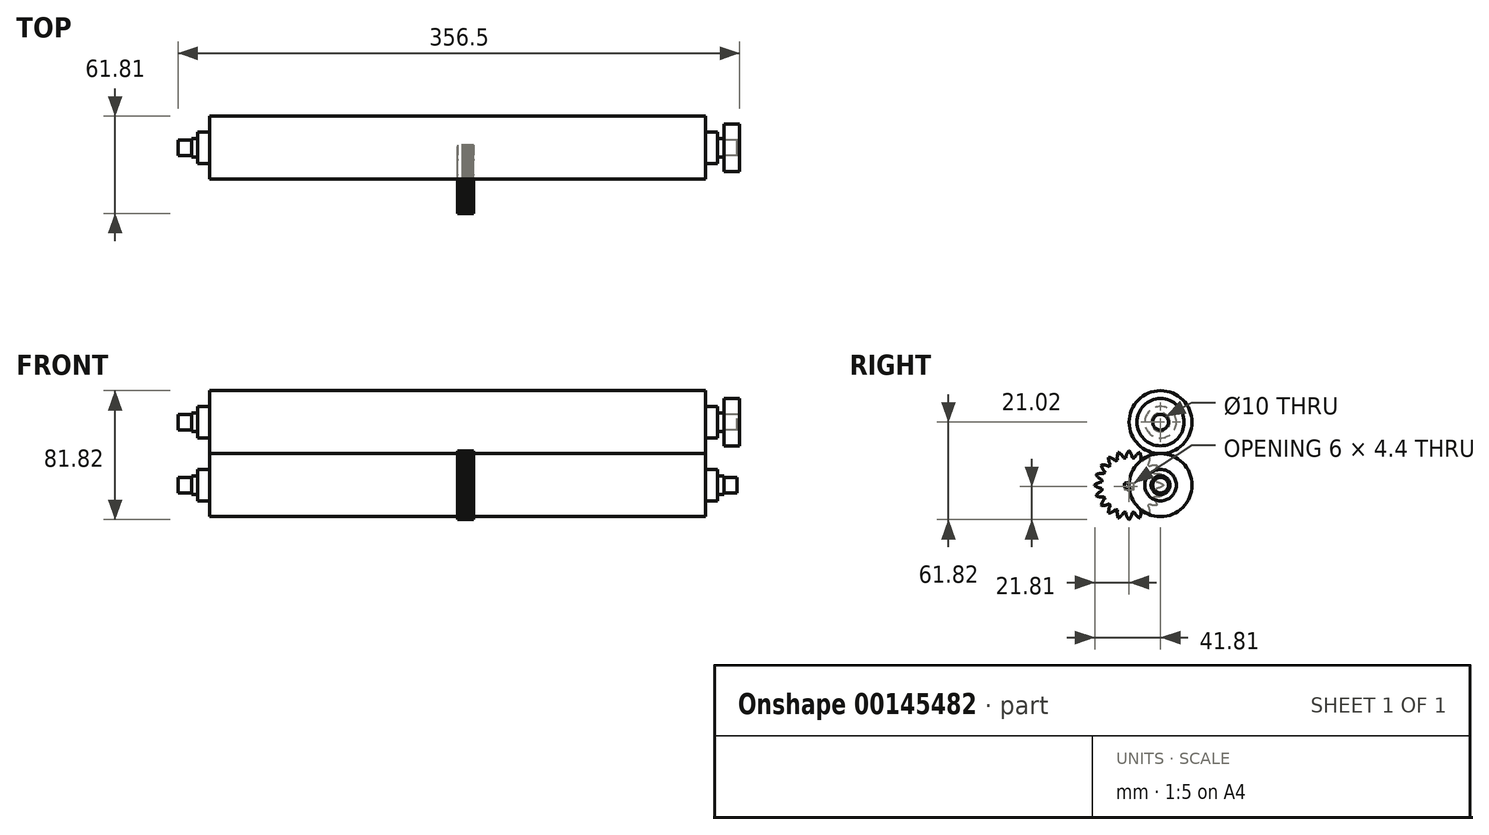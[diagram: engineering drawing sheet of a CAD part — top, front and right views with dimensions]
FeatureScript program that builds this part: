
annotation { "Feature Type Name" : "Feature", "Feature Type Description" : "" }
export const myFeature = defineFeature(function(context is Context, id is Id, definition is map)
    precondition{}
    {
        {
            var Q0;
            Q0=qCreatedBy(makeId("Right.planeOp"),FACE);
            var sketch = newSketch(context, id + "F0", { "sketchPlane" : qUnion([Q0])});
            skCircle(sketch, "E0", {"center": v(0, 0) * mm, "radius": 20 * mm});
            skCircle(sketch, "E1", {"center": v(0, 0) * mm, "radius": 10 * mm});
            skCircle(sketch, "E2", {"center": v(0, 0) * mm, "radius": 5 * mm});
            skCircle(sketch, "E3", {"center": v(0, 0) * mm, "radius": 6 * mm});
            skSolve(sketch);
        }
        {
            var Q0;
            Q0=makeQuery(id+"F0.imprint","IMPRINT",FACE,{"disambiguationData":[TD([[makeQuery(id+"F0.imprint","IMPRINT",EDGE,{"derivedFrom":sQuery(id+"F0.wireOp",EDGE,"E0")}),1.0]])]});
            extrude(context, id + "F1", {"entities" : qUnion([Q0]), "endBound" : BoundingType.SYMMETRIC, "depth" : 315 * mm});
        }
        {
            var Q0;
            Q0=makeQuery(id+"F0.imprint","IMPRINT",FACE,{"disambiguationData":[TD([[makeQuery(id+"F0.imprint","IMPRINT",EDGE,{"derivedFrom":sQuery(id+"F0.wireOp",EDGE,"E1")}),1.0]])]});
            extrude(context, id + "F2", {"entities" : qUnion([Q0]), "operationType" : NewBodyOperationType.ADD, "endBound" : BoundingType.SYMMETRIC, "depth" : 330 * mm});
        }
        {
            var Q0;
            Q0=makeQuery(id+"F0.imprint","IMPRINT",FACE,{"disambiguationData":[TD([[makeQuery(id+"F0.imprint","IMPRINT",EDGE,{"derivedFrom":sQuery(id+"F0.wireOp",EDGE,"E2")}),-1.0]])]});
            extrude(context, id + "F3", {"entities" : qUnion([Q0]), "operationType" : NewBodyOperationType.ADD, "endBound" : BoundingType.SYMMETRIC, "depth" : 338 * mm});
        }
        {
            var Q0;
            Q0=makeQuery(id+"F0.imprint","IMPRINT",FACE,{"disambiguationData":[TD([[makeQuery(id+"F0.imprint","IMPRINT",EDGE,{"derivedFrom":sQuery(id+"F0.wireOp",EDGE,"E2")}),1.0]])]});
            extrude(context, id + "F4", {"entities" : qUnion([Q0]), "operationType" : NewBodyOperationType.ADD, "endBound" : BoundingType.SYMMETRIC, "depth" : 355 * mm});
        }
        {
            var Q0;
            Q0=makeQuery(id+"F1.opExtrude","SWEPT_BODY",BODY,{"disambiguationData":[OSD([sQuery(id+"F0.wireOp",EDGE,"E0"),sQuery(id+"F0.wireOp",EDGE,"E1")])]});
            transform(context, id + "F5", {"entities" : qUnion([Q0]), "transformType" : TransformType.TRANSLATION_3D, "dx" : 0 * mm, "dy" : 0 * mm, "dz" : 40 * mm, "makeCopy" : true});
        }
        {
            var Q0;
            Q0=makeQuery(id+"F3.opExtrude","CAP_FACE",FACE,{"disambiguationData":[OSD([sQuery(id+"F0.wireOp",EDGE,"E2"),sQuery(id+"F0.wireOp",EDGE,"E3")])],"isStart":false});
            var sketch = newSketch(context, id + "F6", { "sketchPlane" : qUnion([Q0])});
            skLineSegment(sketch, "E4", {"start": v(0, 69.94) * mm, "end": v(0, -29.94) * mm, "construction": true});
            skLineSegment(sketch, "E5", {"start": v(-33.24, 0) * mm, "end": v(34.61, 0) * mm, "construction": true});
            skLineSegment(sketch, "E6", {"start": v(-30.84, 40) * mm, "end": v(31.61, 40) * mm, "construction": true});
            skCircle(sketch, "E7", {"center": v(0, 40) * mm, "radius": 5 * mm});
            skCircle(sketch, "E8", {"center": v(0, 0) * mm, "radius": 5 * mm});
            skLineSegment(sketch, "E9", {"start": v(-34.27, 20) * mm, "end": v(43.16, 20) * mm, "construction": true});
            skPoint(sketch, "E9.startSnap0", {"position": v(0, 20) * mm});
            skCircle(sketch, "E10", {"center": v(0, 40) * mm, "radius": 15 * mm});
            skSolve(sketch);
        }
        {
            var Q0;
            Q0=makeQuery(id+"F6.imprint","IMPRINT",FACE,{"disambiguationData":[TD([[makeQuery(id+"F6.imprint","IMPRINT",EDGE,{"derivedFrom":sQuery(id+"F6.wireOp",EDGE,"E7")}),-1.0]])]});
            extrude(context, id + "F7", {"entities" : qUnion([Q0]), "depth" : 10 * mm});
        }
        {
            var Q0;
            Q0=qCreatedBy(makeId("Right.planeOp"),FACE);
            var sketch = newSketch(context, id + "F8", { "sketchPlane" : qUnion([Q0])});
            skCircle(sketch, "E11.cCircle", {"center": v(-47.34, 46.55) * mm, "radius": 11.16 * mm, "construction": true});
            skLineSegment(sketch, "E11.0", {"start": v(-38.6, 37.07) * mm, "end": v(-51.18, 34.24) * mm});
            skLineSegment(sketch, "E11.1", {"start": v(-51.18, 34.24) * mm, "end": v(-59.91, 43.72) * mm});
            skLineSegment(sketch, "E11.2", {"start": v(-59.91, 43.72) * mm, "end": v(-56.07, 56.02) * mm});
            skLineSegment(sketch, "E11.3", {"start": v(-56.07, 56.02) * mm, "end": v(-43.5, 58.85) * mm});
            skLineSegment(sketch, "E11.4", {"start": v(-43.5, 58.85) * mm, "end": v(-34.77, 49.38) * mm});
            skLineSegment(sketch, "E11.5", {"start": v(-34.77, 49.38) * mm, "end": v(-38.6, 37.07) * mm});
            skPoint(sketch, "E11.0.midPoint", {"position": v(-44.89, 35.66) * mm});
            skSolve(sketch);
        }
        {
            var Q0;
            Q0=makeQuery(id+"F8.imprint","IMPRINT",FACE,{"disambiguationData":[TD([[makeQuery(id+"F8.imprint","IMPRINT",EDGE,{"derivedFrom":sQuery(id+"F8.wireOp",EDGE,"E11.0")}),-1.0]])]});
            extrude(context, id + "F9", {"entities" : qUnion([Q0]), "depth" : 25 * mm});
        }
        {
            var Q0;
            Q0=makeQuery(id+"F9.opExtrude","SWEPT_BODY",BODY,{"disambiguationData":[OSD([sQuery(id+"F8.wireOp",EDGE,"E11.0"),sQuery(id+"F8.wireOp",EDGE,"E11.1"),sQuery(id+"F8.wireOp",EDGE,"E11.2"),sQuery(id+"F8.wireOp",EDGE,"E11.3"),sQuery(id+"F8.wireOp",EDGE,"E11.4"),sQuery(id+"F8.wireOp",EDGE,"E11.5")])]});
            transform(context, id + "F10", {"entities" : qUnion([Q0]), "transformType" : TransformType.TRANSLATION_3D, "dx" : -53.2 * mm, "dy" : 0 * mm, "dz" : 0 * mm, "makeCopy" : true});
        }
        {
            var Q0;
            Q0=makeQuery(id+"F10.opPattern","COPY",BODY,{"derivedFrom":makeQuery(id+"F9.opExtrude","SWEPT_BODY",BODY,{"disambiguationData":[OSD([sQuery(id+"F8.wireOp",EDGE,"E11.0"),sQuery(id+"F8.wireOp",EDGE,"E11.1"),sQuery(id+"F8.wireOp",EDGE,"E11.2"),sQuery(id+"F8.wireOp",EDGE,"E11.3"),sQuery(id+"F8.wireOp",EDGE,"E11.4"),sQuery(id+"F8.wireOp",EDGE,"E11.5")])]}),"instanceName":"1"});
            var Q1;
            Q1=makeQuery(id+"F10.opPattern","COPY",EDGE,{"derivedFrom":makeQuery(id+"F9.opExtrude","SWEPT_EDGE",EDGE,{"disambiguationData":[OSD([sQuery(id+"F8.wireOp",EDGE,"E11.0"),sQuery(id+"F8.wireOp",EDGE,"E11.1")])]}),"instanceName":"1"});
            transform(context, id + "F11", {"entities" : qUnion([Q0]), "transformType" : TransformType.ROTATION, "transformAxis" : qUnion([Q1]), "angle" : 30 * degree, "makeCopy" : false});
        }
        {
            var Q0;
            Q0=makeQuery(id+"F10.opPattern","COPY",FACE,{"derivedFrom":makeQuery(id+"F9.opExtrude","CAP_FACE",FACE,{"disambiguationData":[OSD([sQuery(id+"F8.wireOp",EDGE,"E11.0"),sQuery(id+"F8.wireOp",EDGE,"E11.1"),sQuery(id+"F8.wireOp",EDGE,"E11.2"),sQuery(id+"F8.wireOp",EDGE,"E11.3"),sQuery(id+"F8.wireOp",EDGE,"E11.4"),sQuery(id+"F8.wireOp",EDGE,"E11.5")])],"isStart":false}),"instanceName":"1"});
            var Q1;
            Q1=makeQuery(id+"F9.opExtrude","CAP_FACE",FACE,{"disambiguationData":[OSD([sQuery(id+"F8.wireOp",EDGE,"E11.0"),sQuery(id+"F8.wireOp",EDGE,"E11.1"),sQuery(id+"F8.wireOp",EDGE,"E11.2"),sQuery(id+"F8.wireOp",EDGE,"E11.3"),sQuery(id+"F8.wireOp",EDGE,"E11.4"),sQuery(id+"F8.wireOp",EDGE,"E11.5")])],"isStart":true});
            loft(context, id + "F12", {"sheetProfilesArray" : [{ "sheetProfileEntities" : qUnion([Q0]) }, { "sheetProfileEntities" : qUnion([Q1]) }]});
        }
        {
            var Q0;
            Q0=makeQuery(id+"F12.opLoft","SWEPT_BODY",BODY,{"disambiguationData":[OSD([sQuery(id+"F8.wireOp",EDGE,"E11.0"),sQuery(id+"F8.wireOp",EDGE,"E11.1"),sQuery(id+"F8.wireOp",EDGE,"E11.2"),sQuery(id+"F8.wireOp",EDGE,"E11.3"),sQuery(id+"F8.wireOp",EDGE,"E11.4"),sQuery(id+"F8.wireOp",EDGE,"E11.5")])]});
            deleteBodies(context, id + "F13", {"entities" : qUnion([Q0])});
        }
        {
            var Q0;
            Q0=makeQuery(id+"F10.opPattern","COPY",BODY,{"derivedFrom":makeQuery(id+"F9.opExtrude","SWEPT_BODY",BODY,{"disambiguationData":[OSD([sQuery(id+"F8.wireOp",EDGE,"E11.0"),sQuery(id+"F8.wireOp",EDGE,"E11.1"),sQuery(id+"F8.wireOp",EDGE,"E11.2"),sQuery(id+"F8.wireOp",EDGE,"E11.3"),sQuery(id+"F8.wireOp",EDGE,"E11.4"),sQuery(id+"F8.wireOp",EDGE,"E11.5")])]}),"instanceName":"1"});
            deleteBodies(context, id + "F14", {"entities" : qUnion([Q0])});
        }
        {
            var Q0;
            Q0=makeQuery(id+"F9.opExtrude","SWEPT_BODY",BODY,{"disambiguationData":[OSD([sQuery(id+"F8.wireOp",EDGE,"E11.0"),sQuery(id+"F8.wireOp",EDGE,"E11.1"),sQuery(id+"F8.wireOp",EDGE,"E11.2"),sQuery(id+"F8.wireOp",EDGE,"E11.3"),sQuery(id+"F8.wireOp",EDGE,"E11.4"),sQuery(id+"F8.wireOp",EDGE,"E11.5")])]});
            deleteBodies(context, id + "F15", {"entities" : qUnion([Q0])});
        }
        {
            var Q0;
            Q0=qCreatedBy(makeId("Right.planeOp"),FACE);
            var sketch = newSketch(context, id + "F16", { "sketchPlane" : qUnion([Q0])});
            skLineSegment(sketch, "E12", {"start": v(-0.26, 0.2) * mm, "end": v(-0.26, 0.2) * mm});
            skLineSegment(sketch, "E13", {"start": v(-0.26, 0.2) * mm, "end": v(-0.25, 0.2) * mm});
            skLineSegment(sketch, "E14", {"start": v(-0.25, 0.2) * mm, "end": v(-0.24, 0.2) * mm});
            skLineSegment(sketch, "E15", {"start": v(-0.24, 0.2) * mm, "end": v(-0.23, 0.2) * mm});
            skLineSegment(sketch, "E16", {"start": v(-0.23, 0.2) * mm, "end": v(-0.23, 0.2) * mm});
            skLineSegment(sketch, "E17", {"start": v(-0.23, 0.2) * mm, "end": v(-0.22, 0.2) * mm});
            skLineSegment(sketch, "E18", {"start": v(-0.22, 0.2) * mm, "end": v(-0.2, 0.2) * mm});
            skLineSegment(sketch, "E19", {"start": v(-0.2, 0.2) * mm, "end": v(-0.18, 0.2) * mm});
            skLineSegment(sketch, "E20", {"start": v(-0.18, 0.2) * mm, "end": v(-0.17, 0.2) * mm});
            skLineSegment(sketch, "E21", {"start": v(-0.17, 0.2) * mm, "end": v(-0.14, 0.19) * mm});
            skLineSegment(sketch, "E22", {"start": v(-0.14, 0.19) * mm, "end": v(-0.1, 0.18) * mm});
            skLineSegment(sketch, "E23", {"start": v(-0.1, 0.18) * mm, "end": v(-0.07, 0.16) * mm});
            skLineSegment(sketch, "E24", {"start": v(-0.07, 0.16) * mm, "end": v(-0.04, 0.15) * mm});
            skLineSegment(sketch, "E25", {"start": v(-0.04, 0.15) * mm, "end": v(0, 0.14) * mm});
            skLineSegment(sketch, "E26", {"start": v(0, 0.14) * mm, "end": v(0.02, 0.12) * mm});
            skLineSegment(sketch, "E27", {"start": v(0.02, 0.12) * mm, "end": v(0.06, 0.1) * mm});
            skLineSegment(sketch, "E28", {"start": v(0.06, 0.1) * mm, "end": v(0.09, 0.08) * mm});
            skLineSegment(sketch, "E29", {"start": v(0.09, 0.08) * mm, "end": v(0.12, 0.06) * mm});
            skLineSegment(sketch, "E30", {"start": v(0.12, 0.06) * mm, "end": v(0.15, 0.04) * mm});
            skLineSegment(sketch, "E31", {"start": v(0.15, 0.04) * mm, "end": v(0.18, 0.02) * mm});
            skLineSegment(sketch, "E32", {"start": v(0.18, 0.02) * mm, "end": v(0.18, -0.02) * mm});
            skLineSegment(sketch, "E33", {"start": v(0.18, -0.02) * mm, "end": v(0.15, -0.04) * mm});
            skLineSegment(sketch, "E34", {"start": v(0.15, -0.04) * mm, "end": v(0.12, -0.06) * mm});
            skLineSegment(sketch, "E35", {"start": v(0.12, -0.06) * mm, "end": v(0.09, -0.08) * mm});
            skLineSegment(sketch, "E36", {"start": v(0.09, -0.08) * mm, "end": v(0.06, -0.1) * mm});
            skLineSegment(sketch, "E37", {"start": v(0.06, -0.1) * mm, "end": v(0.02, -0.12) * mm});
            skLineSegment(sketch, "E38", {"start": v(0.02, -0.12) * mm, "end": v(0, -0.14) * mm});
            skLineSegment(sketch, "E39", {"start": v(0, -0.14) * mm, "end": v(-0.04, -0.15) * mm});
            skLineSegment(sketch, "E40", {"start": v(-0.04, -0.15) * mm, "end": v(-0.07, -0.16) * mm});
            skLineSegment(sketch, "E41", {"start": v(-0.07, -0.16) * mm, "end": v(-0.1, -0.18) * mm});
            skLineSegment(sketch, "E42", {"start": v(-0.1, -0.18) * mm, "end": v(-0.14, -0.19) * mm});
            skLineSegment(sketch, "E43", {"start": v(-0.14, -0.19) * mm, "end": v(-0.17, -0.2) * mm});
            skLineSegment(sketch, "E44", {"start": v(-0.17, -0.2) * mm, "end": v(-0.18, -0.2) * mm});
            skLineSegment(sketch, "E45", {"start": v(-0.18, -0.2) * mm, "end": v(-0.2, -0.2) * mm});
            skLineSegment(sketch, "E46", {"start": v(-0.2, -0.2) * mm, "end": v(-0.22, -0.2) * mm});
            skLineSegment(sketch, "E47", {"start": v(-0.22, -0.2) * mm, "end": v(-0.23, -0.2) * mm});
            skLineSegment(sketch, "E48", {"start": v(-0.23, -0.2) * mm, "end": v(-0.23, -0.2) * mm});
            skLineSegment(sketch, "E49", {"start": v(-0.23, -0.2) * mm, "end": v(-0.24, -0.2) * mm});
            skLineSegment(sketch, "E50", {"start": v(-0.24, -0.2) * mm, "end": v(-0.25, -0.2) * mm});
            skLineSegment(sketch, "E51", {"start": v(-0.25, -0.2) * mm, "end": v(-0.26, -0.2) * mm});
            skLineSegment(sketch, "E52", {"start": v(-0.26, -0.2) * mm, "end": v(-0.26, -0.2) * mm});
            skLineSegment(sketch, "E53", {"start": v(-0.26, -0.2) * mm, "end": v(-0.29, -0.34) * mm});
            skLineSegment(sketch, "E54", {"start": v(-0.29, -0.34) * mm, "end": v(-0.28, -0.34) * mm});
            skLineSegment(sketch, "E55", {"start": v(-0.28, -0.34) * mm, "end": v(-0.27, -0.34) * mm});
            skLineSegment(sketch, "E56", {"start": v(-0.27, -0.34) * mm, "end": v(-0.26, -0.35) * mm});
            skLineSegment(sketch, "E57", {"start": v(-0.26, -0.35) * mm, "end": v(-0.26, -0.35) * mm});
            skLineSegment(sketch, "E58", {"start": v(-0.26, -0.35) * mm, "end": v(-0.25, -0.35) * mm});
            skLineSegment(sketch, "E59", {"start": v(-0.25, -0.35) * mm, "end": v(-0.24, -0.36) * mm});
            skLineSegment(sketch, "E60", {"start": v(-0.24, -0.36) * mm, "end": v(-0.23, -0.37) * mm});
            skLineSegment(sketch, "E61", {"start": v(-0.23, -0.37) * mm, "end": v(-0.21, -0.38) * mm});
            skLineSegment(sketch, "E62", {"start": v(-0.21, -0.38) * mm, "end": v(-0.2, -0.38) * mm});
            skLineSegment(sketch, "E63", {"start": v(-0.2, -0.38) * mm, "end": v(-0.17, -0.4) * mm});
            skLineSegment(sketch, "E64", {"start": v(-0.17, -0.4) * mm, "end": v(-0.14, -0.42) * mm});
            skLineSegment(sketch, "E65", {"start": v(-0.14, -0.42) * mm, "end": v(-0.12, -0.44) * mm});
            skLineSegment(sketch, "E66", {"start": v(-0.12, -0.44) * mm, "end": v(-0.1, -0.46) * mm});
            skLineSegment(sketch, "E67", {"start": v(-0.1, -0.46) * mm, "end": v(-0.06, -0.49) * mm});
            skLineSegment(sketch, "E68", {"start": v(-0.06, -0.49) * mm, "end": v(-0.04, -0.51) * mm});
            skLineSegment(sketch, "E69", {"start": v(-0.04, -0.51) * mm, "end": v(-0.01, -0.54) * mm});
            skLineSegment(sketch, "E70", {"start": v(-0.01, -0.54) * mm, "end": v(0.01, -0.57) * mm});
            skLineSegment(sketch, "E71", {"start": v(0.01, -0.57) * mm, "end": v(0.03, -0.6) * mm});
            skLineSegment(sketch, "E72", {"start": v(0.03, -0.6) * mm, "end": v(0.06, -0.62) * mm});
            skLineSegment(sketch, "E73", {"start": v(0.06, -0.62) * mm, "end": v(0.08, -0.66) * mm});
            skLineSegment(sketch, "E74", {"start": v(0.08, -0.66) * mm, "end": v(0.07, -0.7) * mm});
            skLineSegment(sketch, "E75", {"start": v(0.07, -0.7) * mm, "end": v(0.03, -0.7) * mm});
            skLineSegment(sketch, "E76", {"start": v(0.03, -0.7) * mm, "end": v(0, -0.71) * mm});
            skLineSegment(sketch, "E77", {"start": v(0, -0.71) * mm, "end": v(-0.04, -0.72) * mm});
            skLineSegment(sketch, "E78", {"start": v(-0.04, -0.72) * mm, "end": v(-0.08, -0.73) * mm});
            skLineSegment(sketch, "E79", {"start": v(-0.08, -0.73) * mm, "end": v(-0.11, -0.74) * mm});
            skLineSegment(sketch, "E80", {"start": v(-0.11, -0.74) * mm, "end": v(-0.15, -0.74) * mm});
            skLineSegment(sketch, "E81", {"start": v(-0.15, -0.74) * mm, "end": v(-0.18, -0.75) * mm});
            skLineSegment(sketch, "E82", {"start": v(-0.18, -0.75) * mm, "end": v(-0.22, -0.75) * mm});
            skLineSegment(sketch, "E83", {"start": v(-0.22, -0.75) * mm, "end": v(-0.25, -0.75) * mm});
            skLineSegment(sketch, "E84", {"start": v(-0.25, -0.75) * mm, "end": v(-0.29, -0.75) * mm});
            skLineSegment(sketch, "E85", {"start": v(-0.29, -0.75) * mm, "end": v(-0.32, -0.75) * mm});
            skLineSegment(sketch, "E86", {"start": v(-0.32, -0.75) * mm, "end": v(-0.33, -0.74) * mm});
            skLineSegment(sketch, "E87", {"start": v(-0.33, -0.74) * mm, "end": v(-0.35, -0.74) * mm});
            skLineSegment(sketch, "E88", {"start": v(-0.35, -0.74) * mm, "end": v(-0.37, -0.74) * mm});
            skLineSegment(sketch, "E89", {"start": v(-0.37, -0.74) * mm, "end": v(-0.38, -0.74) * mm});
            skLineSegment(sketch, "E90", {"start": v(-0.38, -0.74) * mm, "end": v(-0.38, -0.74) * mm});
            skLineSegment(sketch, "E91", {"start": v(-0.38, -0.74) * mm, "end": v(-0.4, -0.74) * mm});
            skLineSegment(sketch, "E92", {"start": v(-0.4, -0.74) * mm, "end": v(-0.4, -0.74) * mm});
            skLineSegment(sketch, "E93", {"start": v(-0.4, -0.74) * mm, "end": v(-0.41, -0.74) * mm});
            skLineSegment(sketch, "E94", {"start": v(-0.41, -0.74) * mm, "end": v(-0.47, -0.85) * mm});
            skLineSegment(sketch, "E95", {"start": v(-0.47, -0.85) * mm, "end": v(-0.47, -0.86) * mm});
            skLineSegment(sketch, "E96", {"start": v(-0.47, -0.86) * mm, "end": v(-0.46, -0.86) * mm});
            skLineSegment(sketch, "E97", {"start": v(-0.46, -0.86) * mm, "end": v(-0.45, -0.87) * mm});
            skLineSegment(sketch, "E98", {"start": v(-0.45, -0.87) * mm, "end": v(-0.45, -0.87) * mm});
            skLineSegment(sketch, "E99", {"start": v(-0.45, -0.87) * mm, "end": v(-0.44, -0.88) * mm});
            skLineSegment(sketch, "E100", {"start": v(-0.44, -0.88) * mm, "end": v(-0.44, -0.88) * mm});
            skLineSegment(sketch, "E101", {"start": v(-0.44, -0.88) * mm, "end": v(-0.43, -0.9) * mm});
            skLineSegment(sketch, "E102", {"start": v(-0.43, -0.9) * mm, "end": v(-0.42, -0.91) * mm});
            skLineSegment(sketch, "E103", {"start": v(-0.42, -0.91) * mm, "end": v(-0.4, -0.92) * mm});
            skLineSegment(sketch, "E104", {"start": v(-0.4, -0.92) * mm, "end": v(-0.38, -0.94) * mm});
            skLineSegment(sketch, "E105", {"start": v(-0.38, -0.94) * mm, "end": v(-0.36, -0.97) * mm});
            skLineSegment(sketch, "E106", {"start": v(-0.36, -0.97) * mm, "end": v(-0.34, -1) * mm});
            skLineSegment(sketch, "E107", {"start": v(-0.34, -1) * mm, "end": v(-0.33, -1.03) * mm});
            skLineSegment(sketch, "E108", {"start": v(-0.33, -1.03) * mm, "end": v(-0.3, -1.06) * mm});
            skLineSegment(sketch, "E109", {"start": v(-0.3, -1.06) * mm, "end": v(-0.3, -1.1) * mm});
            skLineSegment(sketch, "E110", {"start": v(-0.3, -1.1) * mm, "end": v(-0.28, -1.13) * mm});
            skLineSegment(sketch, "E111", {"start": v(-0.28, -1.13) * mm, "end": v(-0.26, -1.16) * mm});
            skLineSegment(sketch, "E112", {"start": v(-0.26, -1.16) * mm, "end": v(-0.25, -1.2) * mm});
            skLineSegment(sketch, "E113", {"start": v(-0.25, -1.2) * mm, "end": v(-0.24, -1.23) * mm});
            skLineSegment(sketch, "E114", {"start": v(-0.24, -1.23) * mm, "end": v(-0.22, -1.27) * mm});
            skLineSegment(sketch, "E115", {"start": v(-0.22, -1.27) * mm, "end": v(-0.25, -1.3) * mm});
            skLineSegment(sketch, "E116", {"start": v(-0.25, -1.3) * mm, "end": v(-0.28, -1.3) * mm});
            skLineSegment(sketch, "E117", {"start": v(-0.28, -1.3) * mm, "end": v(-0.32, -1.3) * mm});
            skLineSegment(sketch, "E118", {"start": v(-0.32, -1.3) * mm, "end": v(-0.36, -1.3) * mm});
            skLineSegment(sketch, "E119", {"start": v(-0.36, -1.3) * mm, "end": v(-0.4, -1.3) * mm});
            skLineSegment(sketch, "E120", {"start": v(-0.4, -1.3) * mm, "end": v(-0.43, -1.29) * mm});
            skLineSegment(sketch, "E121", {"start": v(-0.43, -1.29) * mm, "end": v(-0.47, -1.28) * mm});
            skLineSegment(sketch, "E122", {"start": v(-0.47, -1.28) * mm, "end": v(-0.5, -1.27) * mm});
            skLineSegment(sketch, "E123", {"start": v(-0.5, -1.27) * mm, "end": v(-0.54, -1.27) * mm});
            skLineSegment(sketch, "E124", {"start": v(-0.54, -1.27) * mm, "end": v(-0.57, -1.26) * mm});
            skLineSegment(sketch, "E125", {"start": v(-0.57, -1.26) * mm, "end": v(-0.6, -1.25) * mm});
            skLineSegment(sketch, "E126", {"start": v(-0.6, -1.25) * mm, "end": v(-0.63, -1.23) * mm});
            skLineSegment(sketch, "E127", {"start": v(-0.63, -1.23) * mm, "end": v(-0.64, -1.22) * mm});
            skLineSegment(sketch, "E128", {"start": v(-0.64, -1.22) * mm, "end": v(-0.66, -1.22) * mm});
            skLineSegment(sketch, "E129", {"start": v(-0.66, -1.22) * mm, "end": v(-0.68, -1.21) * mm});
            skLineSegment(sketch, "E130", {"start": v(-0.68, -1.21) * mm, "end": v(-0.68, -1.2) * mm});
            skLineSegment(sketch, "E131", {"start": v(-0.68, -1.2) * mm, "end": v(-0.7, -1.2) * mm});
            skLineSegment(sketch, "E132", {"start": v(-0.7, -1.2) * mm, "end": v(-0.7, -1.2) * mm});
            skLineSegment(sketch, "E133", {"start": v(-0.7, -1.2) * mm, "end": v(-0.71, -1.2) * mm});
            skLineSegment(sketch, "E134", {"start": v(-0.71, -1.2) * mm, "end": v(-0.72, -1.19) * mm});
            skLineSegment(sketch, "E135", {"start": v(-0.72, -1.19) * mm, "end": v(-0.81, -1.28) * mm});
            skLineSegment(sketch, "E136", {"start": v(-0.81, -1.28) * mm, "end": v(-0.8, -1.29) * mm});
            skLineSegment(sketch, "E137", {"start": v(-0.8, -1.29) * mm, "end": v(-0.8, -1.3) * mm});
            skLineSegment(sketch, "E138", {"start": v(-0.8, -1.3) * mm, "end": v(-0.8, -1.3) * mm});
            skLineSegment(sketch, "E139", {"start": v(-0.8, -1.3) * mm, "end": v(-0.8, -1.32) * mm});
            skLineSegment(sketch, "E140", {"start": v(-0.8, -1.32) * mm, "end": v(-0.79, -1.32) * mm});
            skLineSegment(sketch, "E141", {"start": v(-0.79, -1.32) * mm, "end": v(-0.78, -1.34) * mm});
            skLineSegment(sketch, "E142", {"start": v(-0.78, -1.34) * mm, "end": v(-0.78, -1.36) * mm});
            skLineSegment(sketch, "E143", {"start": v(-0.78, -1.36) * mm, "end": v(-0.77, -1.37) * mm});
            skLineSegment(sketch, "E144", {"start": v(-0.77, -1.37) * mm, "end": v(-0.75, -1.4) * mm});
            skLineSegment(sketch, "E145", {"start": v(-0.75, -1.4) * mm, "end": v(-0.74, -1.43) * mm});
            skLineSegment(sketch, "E146", {"start": v(-0.74, -1.43) * mm, "end": v(-0.73, -1.46) * mm});
            skLineSegment(sketch, "E147", {"start": v(-0.73, -1.46) * mm, "end": v(-0.73, -1.5) * mm});
            skLineSegment(sketch, "E148", {"start": v(-0.73, -1.5) * mm, "end": v(-0.72, -1.53) * mm});
            skLineSegment(sketch, "E149", {"start": v(-0.72, -1.53) * mm, "end": v(-0.71, -1.57) * mm});
            skLineSegment(sketch, "E150", {"start": v(-0.71, -1.57) * mm, "end": v(-0.7, -1.6) * mm});
            skLineSegment(sketch, "E151", {"start": v(-0.7, -1.6) * mm, "end": v(-0.7, -1.64) * mm});
            skLineSegment(sketch, "E152", {"start": v(-0.7, -1.64) * mm, "end": v(-0.7, -1.68) * mm});
            skLineSegment(sketch, "E153", {"start": v(-0.7, -1.68) * mm, "end": v(-0.7, -1.72) * mm});
            skLineSegment(sketch, "E154", {"start": v(-0.7, -1.72) * mm, "end": v(-0.7, -1.75) * mm});
            skLineSegment(sketch, "E155", {"start": v(-0.7, -1.75) * mm, "end": v(-0.73, -1.78) * mm});
            skLineSegment(sketch, "E156", {"start": v(-0.73, -1.78) * mm, "end": v(-0.77, -1.76) * mm});
            skLineSegment(sketch, "E157", {"start": v(-0.77, -1.76) * mm, "end": v(-0.8, -1.75) * mm});
            skLineSegment(sketch, "E158", {"start": v(-0.8, -1.75) * mm, "end": v(-0.84, -1.74) * mm});
            skLineSegment(sketch, "E159", {"start": v(-0.84, -1.74) * mm, "end": v(-0.87, -1.72) * mm});
            skLineSegment(sketch, "E160", {"start": v(-0.87, -1.72) * mm, "end": v(-0.9, -1.7) * mm});
            skLineSegment(sketch, "E161", {"start": v(-0.9, -1.7) * mm, "end": v(-0.94, -1.7) * mm});
            skLineSegment(sketch, "E162", {"start": v(-0.94, -1.7) * mm, "end": v(-0.97, -1.67) * mm});
            skLineSegment(sketch, "E163", {"start": v(-0.97, -1.67) * mm, "end": v(-1, -1.66) * mm});
            skLineSegment(sketch, "E164", {"start": v(-1, -1.66) * mm, "end": v(-1.03, -1.64) * mm});
            skLineSegment(sketch, "E165", {"start": v(-1.03, -1.64) * mm, "end": v(-1.06, -1.62) * mm});
            skLineSegment(sketch, "E166", {"start": v(-1.06, -1.62) * mm, "end": v(-1.08, -1.6) * mm});
            skLineSegment(sketch, "E167", {"start": v(-1.08, -1.6) * mm, "end": v(-1.09, -1.58) * mm});
            skLineSegment(sketch, "E168", {"start": v(-1.09, -1.58) * mm, "end": v(-1.1, -1.57) * mm});
            skLineSegment(sketch, "E169", {"start": v(-1.1, -1.57) * mm, "end": v(-1.12, -1.56) * mm});
            skLineSegment(sketch, "E170", {"start": v(-1.12, -1.56) * mm, "end": v(-1.12, -1.56) * mm});
            skLineSegment(sketch, "E171", {"start": v(-1.12, -1.56) * mm, "end": v(-1.13, -1.55) * mm});
            skLineSegment(sketch, "E172", {"start": v(-1.13, -1.55) * mm, "end": v(-1.13, -1.55) * mm});
            skLineSegment(sketch, "E173", {"start": v(-1.13, -1.55) * mm, "end": v(-1.14, -1.54) * mm});
            skLineSegment(sketch, "E174", {"start": v(-1.14, -1.54) * mm, "end": v(-1.14, -1.53) * mm});
            skLineSegment(sketch, "E175", {"start": v(-1.14, -1.53) * mm, "end": v(-1.15, -1.53) * mm});
            skLineSegment(sketch, "E176", {"start": v(-1.15, -1.53) * mm, "end": v(-1.26, -1.59) * mm});
            skLineSegment(sketch, "E177", {"start": v(-1.26, -1.59) * mm, "end": v(-1.26, -1.6) * mm});
            skLineSegment(sketch, "E178", {"start": v(-1.26, -1.6) * mm, "end": v(-1.26, -1.6) * mm});
            skLineSegment(sketch, "E179", {"start": v(-1.26, -1.6) * mm, "end": v(-1.26, -1.62) * mm});
            skLineSegment(sketch, "E180", {"start": v(-1.26, -1.62) * mm, "end": v(-1.26, -1.62) * mm});
            skLineSegment(sketch, "E181", {"start": v(-1.26, -1.62) * mm, "end": v(-1.26, -1.63) * mm});
            skLineSegment(sketch, "E182", {"start": v(-1.26, -1.63) * mm, "end": v(-1.26, -1.65) * mm});
            skLineSegment(sketch, "E183", {"start": v(-1.26, -1.65) * mm, "end": v(-1.26, -1.67) * mm});
            skLineSegment(sketch, "E184", {"start": v(-1.26, -1.67) * mm, "end": v(-1.25, -1.68) * mm});
            skLineSegment(sketch, "E185", {"start": v(-1.25, -1.68) * mm, "end": v(-1.25, -1.71) * mm});
            skLineSegment(sketch, "E186", {"start": v(-1.25, -1.71) * mm, "end": v(-1.25, -1.75) * mm});
            skLineSegment(sketch, "E187", {"start": v(-1.25, -1.75) * mm, "end": v(-1.25, -1.78) * mm});
            skLineSegment(sketch, "E188", {"start": v(-1.25, -1.78) * mm, "end": v(-1.25, -1.82) * mm});
            skLineSegment(sketch, "E189", {"start": v(-1.25, -1.82) * mm, "end": v(-1.26, -1.85) * mm});
            skLineSegment(sketch, "E190", {"start": v(-1.26, -1.85) * mm, "end": v(-1.26, -1.89) * mm});
            skLineSegment(sketch, "E191", {"start": v(-1.26, -1.89) * mm, "end": v(-1.27, -1.92) * mm});
            skLineSegment(sketch, "E192", {"start": v(-1.27, -1.92) * mm, "end": v(-1.28, -1.96) * mm});
            skLineSegment(sketch, "E193", {"start": v(-1.28, -1.96) * mm, "end": v(-1.29, -2) * mm});
            skLineSegment(sketch, "E194", {"start": v(-1.29, -2) * mm, "end": v(-1.3, -2.03) * mm});
            skLineSegment(sketch, "E195", {"start": v(-1.3, -2.03) * mm, "end": v(-1.3, -2.07) * mm});
            skLineSegment(sketch, "E196", {"start": v(-1.3, -2.07) * mm, "end": v(-1.34, -2.08) * mm});
            skLineSegment(sketch, "E197", {"start": v(-1.34, -2.08) * mm, "end": v(-1.38, -2.06) * mm});
            skLineSegment(sketch, "E198", {"start": v(-1.38, -2.06) * mm, "end": v(-1.4, -2.03) * mm});
            skLineSegment(sketch, "E199", {"start": v(-1.4, -2.03) * mm, "end": v(-1.43, -2.01) * mm});
            skLineSegment(sketch, "E200", {"start": v(-1.43, -2.01) * mm, "end": v(-1.46, -1.99) * mm});
            skLineSegment(sketch, "E201", {"start": v(-1.46, -1.99) * mm, "end": v(-1.49, -1.96) * mm});
            skLineSegment(sketch, "E202", {"start": v(-1.49, -1.96) * mm, "end": v(-1.51, -1.94) * mm});
            skLineSegment(sketch, "E203", {"start": v(-1.51, -1.94) * mm, "end": v(-1.54, -1.9) * mm});
            skLineSegment(sketch, "E204", {"start": v(-1.54, -1.9) * mm, "end": v(-1.56, -1.88) * mm});
            skLineSegment(sketch, "E205", {"start": v(-1.56, -1.88) * mm, "end": v(-1.58, -1.86) * mm});
            skLineSegment(sketch, "E206", {"start": v(-1.58, -1.86) * mm, "end": v(-1.6, -1.83) * mm});
            skLineSegment(sketch, "E207", {"start": v(-1.6, -1.83) * mm, "end": v(-1.62, -1.8) * mm});
            skLineSegment(sketch, "E208", {"start": v(-1.62, -1.8) * mm, "end": v(-1.62, -1.79) * mm});
            skLineSegment(sketch, "E209", {"start": v(-1.62, -1.79) * mm, "end": v(-1.63, -1.77) * mm});
            skLineSegment(sketch, "E210", {"start": v(-1.63, -1.77) * mm, "end": v(-1.64, -1.76) * mm});
            skLineSegment(sketch, "E211", {"start": v(-1.64, -1.76) * mm, "end": v(-1.65, -1.75) * mm});
            skLineSegment(sketch, "E212", {"start": v(-1.65, -1.75) * mm, "end": v(-1.65, -1.74) * mm});
            skLineSegment(sketch, "E213", {"start": v(-1.65, -1.74) * mm, "end": v(-1.65, -1.74) * mm});
            skLineSegment(sketch, "E214", {"start": v(-1.65, -1.74) * mm, "end": v(-1.66, -1.73) * mm});
            skLineSegment(sketch, "E215", {"start": v(-1.66, -1.73) * mm, "end": v(-1.66, -1.72) * mm});
            skLineSegment(sketch, "E216", {"start": v(-1.66, -1.72) * mm, "end": v(-1.66, -1.71) * mm});
            skLineSegment(sketch, "E217", {"start": v(-1.66, -1.71) * mm, "end": v(-1.8, -1.74) * mm});
            skLineSegment(sketch, "E218", {"start": v(-1.8, -1.74) * mm, "end": v(-1.8, -1.74) * mm});
            skLineSegment(sketch, "E219", {"start": v(-1.8, -1.74) * mm, "end": v(-1.8, -1.75) * mm});
            skLineSegment(sketch, "E220", {"start": v(-1.8, -1.75) * mm, "end": v(-1.8, -1.76) * mm});
            skLineSegment(sketch, "E221", {"start": v(-1.8, -1.76) * mm, "end": v(-1.8, -1.77) * mm});
            skLineSegment(sketch, "E222", {"start": v(-1.8, -1.77) * mm, "end": v(-1.8, -1.77) * mm});
            skLineSegment(sketch, "E223", {"start": v(-1.8, -1.77) * mm, "end": v(-1.8, -1.78) * mm});
            skLineSegment(sketch, "E224", {"start": v(-1.8, -1.78) * mm, "end": v(-1.8, -1.8) * mm});
            skLineSegment(sketch, "E225", {"start": v(-1.8, -1.8) * mm, "end": v(-1.8, -1.82) * mm});
            skLineSegment(sketch, "E226", {"start": v(-1.8, -1.82) * mm, "end": v(-1.8, -1.83) * mm});
            skLineSegment(sketch, "E227", {"start": v(-1.8, -1.83) * mm, "end": v(-1.81, -1.86) * mm});
            skLineSegment(sketch, "E228", {"start": v(-1.81, -1.86) * mm, "end": v(-1.82, -1.9) * mm});
            skLineSegment(sketch, "E229", {"start": v(-1.82, -1.9) * mm, "end": v(-1.84, -1.93) * mm});
            skLineSegment(sketch, "E230", {"start": v(-1.84, -1.93) * mm, "end": v(-1.85, -1.96) * mm});
            skLineSegment(sketch, "E231", {"start": v(-1.85, -1.96) * mm, "end": v(-1.86, -2) * mm});
            skLineSegment(sketch, "E232", {"start": v(-1.86, -2) * mm, "end": v(-1.88, -2.02) * mm});
            skLineSegment(sketch, "E233", {"start": v(-1.88, -2.02) * mm, "end": v(-1.9, -2.06) * mm});
            skLineSegment(sketch, "E234", {"start": v(-1.9, -2.06) * mm, "end": v(-1.92, -2.09) * mm});
            skLineSegment(sketch, "E235", {"start": v(-1.92, -2.09) * mm, "end": v(-1.94, -2.12) * mm});
            skLineSegment(sketch, "E236", {"start": v(-1.94, -2.12) * mm, "end": v(-1.96, -2.15) * mm});
            skLineSegment(sketch, "E237", {"start": v(-1.96, -2.15) * mm, "end": v(-1.98, -2.18) * mm});
            skLineSegment(sketch, "E238", {"start": v(-1.98, -2.18) * mm, "end": v(-2.02, -2.18) * mm});
            skLineSegment(sketch, "E239", {"start": v(-2.02, -2.18) * mm, "end": v(-2.04, -2.15) * mm});
            skLineSegment(sketch, "E240", {"start": v(-2.04, -2.15) * mm, "end": v(-2.06, -2.12) * mm});
            skLineSegment(sketch, "E241", {"start": v(-2.06, -2.12) * mm, "end": v(-2.08, -2.09) * mm});
            skLineSegment(sketch, "E242", {"start": v(-2.08, -2.09) * mm, "end": v(-2.1, -2.06) * mm});
            skLineSegment(sketch, "E243", {"start": v(-2.1, -2.06) * mm, "end": v(-2.12, -2.02) * mm});
            skLineSegment(sketch, "E244", {"start": v(-2.12, -2.02) * mm, "end": v(-2.14, -2) * mm});
            skLineSegment(sketch, "E245", {"start": v(-2.14, -2) * mm, "end": v(-2.15, -1.96) * mm});
            skLineSegment(sketch, "E246", {"start": v(-2.15, -1.96) * mm, "end": v(-2.16, -1.93) * mm});
            skLineSegment(sketch, "E247", {"start": v(-2.16, -1.93) * mm, "end": v(-2.18, -1.9) * mm});
            skLineSegment(sketch, "E248", {"start": v(-2.18, -1.9) * mm, "end": v(-2.19, -1.86) * mm});
            skLineSegment(sketch, "E249", {"start": v(-2.19, -1.86) * mm, "end": v(-2.2, -1.83) * mm});
            skLineSegment(sketch, "E250", {"start": v(-2.2, -1.83) * mm, "end": v(-2.2, -1.82) * mm});
            skLineSegment(sketch, "E251", {"start": v(-2.2, -1.82) * mm, "end": v(-2.2, -1.8) * mm});
            skLineSegment(sketch, "E252", {"start": v(-2.2, -1.8) * mm, "end": v(-2.2, -1.78) * mm});
            skLineSegment(sketch, "E253", {"start": v(-2.2, -1.78) * mm, "end": v(-2.2, -1.77) * mm});
            skLineSegment(sketch, "E254", {"start": v(-2.2, -1.77) * mm, "end": v(-2.2, -1.77) * mm});
            skLineSegment(sketch, "E255", {"start": v(-2.2, -1.77) * mm, "end": v(-2.2, -1.76) * mm});
            skLineSegment(sketch, "E256", {"start": v(-2.2, -1.76) * mm, "end": v(-2.2, -1.75) * mm});
            skLineSegment(sketch, "E257", {"start": v(-2.2, -1.75) * mm, "end": v(-2.2, -1.74) * mm});
            skLineSegment(sketch, "E258", {"start": v(-2.2, -1.74) * mm, "end": v(-2.2, -1.74) * mm});
            skLineSegment(sketch, "E259", {"start": v(-2.2, -1.74) * mm, "end": v(-2.34, -1.71) * mm});
            skLineSegment(sketch, "E260", {"start": v(-2.34, -1.71) * mm, "end": v(-2.34, -1.72) * mm});
            skLineSegment(sketch, "E261", {"start": v(-2.34, -1.72) * mm, "end": v(-2.34, -1.73) * mm});
            skLineSegment(sketch, "E262", {"start": v(-2.34, -1.73) * mm, "end": v(-2.35, -1.74) * mm});
            skLineSegment(sketch, "E263", {"start": v(-2.35, -1.74) * mm, "end": v(-2.35, -1.74) * mm});
            skLineSegment(sketch, "E264", {"start": v(-2.35, -1.74) * mm, "end": v(-2.35, -1.75) * mm});
            skLineSegment(sketch, "E265", {"start": v(-2.35, -1.75) * mm, "end": v(-2.36, -1.76) * mm});
            skLineSegment(sketch, "E266", {"start": v(-2.36, -1.76) * mm, "end": v(-2.37, -1.77) * mm});
            skLineSegment(sketch, "E267", {"start": v(-2.37, -1.77) * mm, "end": v(-2.38, -1.79) * mm});
            skLineSegment(sketch, "E268", {"start": v(-2.38, -1.79) * mm, "end": v(-2.38, -1.8) * mm});
            skLineSegment(sketch, "E269", {"start": v(-2.38, -1.8) * mm, "end": v(-2.4, -1.83) * mm});
            skLineSegment(sketch, "E270", {"start": v(-2.4, -1.83) * mm, "end": v(-2.42, -1.86) * mm});
            skLineSegment(sketch, "E271", {"start": v(-2.42, -1.86) * mm, "end": v(-2.44, -1.88) * mm});
            skLineSegment(sketch, "E272", {"start": v(-2.44, -1.88) * mm, "end": v(-2.46, -1.9) * mm});
            skLineSegment(sketch, "E273", {"start": v(-2.46, -1.9) * mm, "end": v(-2.49, -1.94) * mm});
            skLineSegment(sketch, "E274", {"start": v(-2.49, -1.94) * mm, "end": v(-2.51, -1.96) * mm});
            skLineSegment(sketch, "E275", {"start": v(-2.51, -1.96) * mm, "end": v(-2.54, -1.99) * mm});
            skLineSegment(sketch, "E276", {"start": v(-2.54, -1.99) * mm, "end": v(-2.57, -2.01) * mm});
            skLineSegment(sketch, "E277", {"start": v(-2.57, -2.01) * mm, "end": v(-2.6, -2.03) * mm});
            skLineSegment(sketch, "E278", {"start": v(-2.6, -2.03) * mm, "end": v(-2.62, -2.06) * mm});
            skLineSegment(sketch, "E279", {"start": v(-2.62, -2.06) * mm, "end": v(-2.66, -2.08) * mm});
            skLineSegment(sketch, "E280", {"start": v(-2.66, -2.08) * mm, "end": v(-2.7, -2.07) * mm});
            skLineSegment(sketch, "E281", {"start": v(-2.7, -2.07) * mm, "end": v(-2.7, -2.03) * mm});
            skLineSegment(sketch, "E282", {"start": v(-2.7, -2.03) * mm, "end": v(-2.71, -2) * mm});
            skLineSegment(sketch, "E283", {"start": v(-2.71, -2) * mm, "end": v(-2.72, -1.96) * mm});
            skLineSegment(sketch, "E284", {"start": v(-2.72, -1.96) * mm, "end": v(-2.73, -1.92) * mm});
            skLineSegment(sketch, "E285", {"start": v(-2.73, -1.92) * mm, "end": v(-2.74, -1.89) * mm});
            skLineSegment(sketch, "E286", {"start": v(-2.74, -1.89) * mm, "end": v(-2.74, -1.85) * mm});
            skLineSegment(sketch, "E287", {"start": v(-2.74, -1.85) * mm, "end": v(-2.75, -1.82) * mm});
            skLineSegment(sketch, "E288", {"start": v(-2.75, -1.82) * mm, "end": v(-2.75, -1.78) * mm});
            skLineSegment(sketch, "E289", {"start": v(-2.75, -1.78) * mm, "end": v(-2.75, -1.75) * mm});
            skLineSegment(sketch, "E290", {"start": v(-2.75, -1.75) * mm, "end": v(-2.75, -1.71) * mm});
            skLineSegment(sketch, "E291", {"start": v(-2.75, -1.71) * mm, "end": v(-2.75, -1.68) * mm});
            skLineSegment(sketch, "E292", {"start": v(-2.75, -1.68) * mm, "end": v(-2.74, -1.67) * mm});
            skLineSegment(sketch, "E293", {"start": v(-2.74, -1.67) * mm, "end": v(-2.74, -1.65) * mm});
            skLineSegment(sketch, "E294", {"start": v(-2.74, -1.65) * mm, "end": v(-2.74, -1.63) * mm});
            skLineSegment(sketch, "E295", {"start": v(-2.74, -1.63) * mm, "end": v(-2.74, -1.62) * mm});
            skLineSegment(sketch, "E296", {"start": v(-2.74, -1.62) * mm, "end": v(-2.74, -1.62) * mm});
            skLineSegment(sketch, "E297", {"start": v(-2.74, -1.62) * mm, "end": v(-2.74, -1.6) * mm});
            skLineSegment(sketch, "E298", {"start": v(-2.74, -1.6) * mm, "end": v(-2.74, -1.6) * mm});
            skLineSegment(sketch, "E299", {"start": v(-2.74, -1.6) * mm, "end": v(-2.74, -1.59) * mm});
            skLineSegment(sketch, "E300", {"start": v(-2.74, -1.59) * mm, "end": v(-2.85, -1.53) * mm});
            skLineSegment(sketch, "E301", {"start": v(-2.85, -1.53) * mm, "end": v(-2.86, -1.53) * mm});
            skLineSegment(sketch, "E302", {"start": v(-2.86, -1.53) * mm, "end": v(-2.86, -1.54) * mm});
            skLineSegment(sketch, "E303", {"start": v(-2.86, -1.54) * mm, "end": v(-2.87, -1.55) * mm});
            skLineSegment(sketch, "E304", {"start": v(-2.87, -1.55) * mm, "end": v(-2.87, -1.55) * mm});
            skLineSegment(sketch, "E305", {"start": v(-2.87, -1.55) * mm, "end": v(-2.88, -1.56) * mm});
            skLineSegment(sketch, "E306", {"start": v(-2.88, -1.56) * mm, "end": v(-2.88, -1.56) * mm});
            skLineSegment(sketch, "E307", {"start": v(-2.88, -1.56) * mm, "end": v(-2.9, -1.57) * mm});
            skLineSegment(sketch, "E308", {"start": v(-2.9, -1.57) * mm, "end": v(-2.91, -1.58) * mm});
            skLineSegment(sketch, "E309", {"start": v(-2.91, -1.58) * mm, "end": v(-2.92, -1.6) * mm});
            skLineSegment(sketch, "E310", {"start": v(-2.92, -1.6) * mm, "end": v(-2.94, -1.62) * mm});
            skLineSegment(sketch, "E311", {"start": v(-2.94, -1.62) * mm, "end": v(-2.97, -1.64) * mm});
            skLineSegment(sketch, "E312", {"start": v(-2.97, -1.64) * mm, "end": v(-3, -1.66) * mm});
            skLineSegment(sketch, "E313", {"start": v(-3, -1.66) * mm, "end": v(-3.03, -1.67) * mm});
            skLineSegment(sketch, "E314", {"start": v(-3.03, -1.67) * mm, "end": v(-3.06, -1.7) * mm});
            skLineSegment(sketch, "E315", {"start": v(-3.06, -1.7) * mm, "end": v(-3.1, -1.7) * mm});
            skLineSegment(sketch, "E316", {"start": v(-3.1, -1.7) * mm, "end": v(-3.13, -1.72) * mm});
            skLineSegment(sketch, "E317", {"start": v(-3.13, -1.72) * mm, "end": v(-3.16, -1.74) * mm});
            skLineSegment(sketch, "E318", {"start": v(-3.16, -1.74) * mm, "end": v(-3.2, -1.75) * mm});
            skLineSegment(sketch, "E319", {"start": v(-3.2, -1.75) * mm, "end": v(-3.23, -1.76) * mm});
            skLineSegment(sketch, "E320", {"start": v(-3.23, -1.76) * mm, "end": v(-3.27, -1.78) * mm});
            skLineSegment(sketch, "E321", {"start": v(-3.27, -1.78) * mm, "end": v(-3.3, -1.75) * mm});
            skLineSegment(sketch, "E322", {"start": v(-3.3, -1.75) * mm, "end": v(-3.3, -1.72) * mm});
            skLineSegment(sketch, "E323", {"start": v(-3.3, -1.72) * mm, "end": v(-3.3, -1.68) * mm});
            skLineSegment(sketch, "E324", {"start": v(-3.3, -1.68) * mm, "end": v(-3.3, -1.64) * mm});
            skLineSegment(sketch, "E325", {"start": v(-3.3, -1.64) * mm, "end": v(-3.3, -1.6) * mm});
            skLineSegment(sketch, "E326", {"start": v(-3.3, -1.6) * mm, "end": v(-3.29, -1.57) * mm});
            skLineSegment(sketch, "E327", {"start": v(-3.29, -1.57) * mm, "end": v(-3.28, -1.53) * mm});
            skLineSegment(sketch, "E328", {"start": v(-3.28, -1.53) * mm, "end": v(-3.27, -1.5) * mm});
            skLineSegment(sketch, "E329", {"start": v(-3.27, -1.5) * mm, "end": v(-3.27, -1.46) * mm});
            skLineSegment(sketch, "E330", {"start": v(-3.27, -1.46) * mm, "end": v(-3.26, -1.43) * mm});
            skLineSegment(sketch, "E331", {"start": v(-3.26, -1.43) * mm, "end": v(-3.25, -1.4) * mm});
            skLineSegment(sketch, "E332", {"start": v(-3.25, -1.4) * mm, "end": v(-3.23, -1.37) * mm});
            skLineSegment(sketch, "E333", {"start": v(-3.23, -1.37) * mm, "end": v(-3.22, -1.36) * mm});
            skLineSegment(sketch, "E334", {"start": v(-3.22, -1.36) * mm, "end": v(-3.22, -1.34) * mm});
            skLineSegment(sketch, "E335", {"start": v(-3.22, -1.34) * mm, "end": v(-3.21, -1.32) * mm});
            skLineSegment(sketch, "E336", {"start": v(-3.21, -1.32) * mm, "end": v(-3.2, -1.32) * mm});
            skLineSegment(sketch, "E337", {"start": v(-3.2, -1.32) * mm, "end": v(-3.2, -1.3) * mm});
            skLineSegment(sketch, "E338", {"start": v(-3.2, -1.3) * mm, "end": v(-3.2, -1.3) * mm});
            skLineSegment(sketch, "E339", {"start": v(-3.2, -1.3) * mm, "end": v(-3.2, -1.29) * mm});
            skLineSegment(sketch, "E340", {"start": v(-3.2, -1.29) * mm, "end": v(-3.19, -1.28) * mm});
            skLineSegment(sketch, "E341", {"start": v(-3.19, -1.28) * mm, "end": v(-3.28, -1.19) * mm});
            skLineSegment(sketch, "E342", {"start": v(-3.28, -1.19) * mm, "end": v(-3.29, -1.2) * mm});
            skLineSegment(sketch, "E343", {"start": v(-3.29, -1.2) * mm, "end": v(-3.3, -1.2) * mm});
            skLineSegment(sketch, "E344", {"start": v(-3.3, -1.2) * mm, "end": v(-3.3, -1.2) * mm});
            skLineSegment(sketch, "E345", {"start": v(-3.3, -1.2) * mm, "end": v(-3.32, -1.2) * mm});
            skLineSegment(sketch, "E346", {"start": v(-3.32, -1.2) * mm, "end": v(-3.32, -1.21) * mm});
            skLineSegment(sketch, "E347", {"start": v(-3.32, -1.21) * mm, "end": v(-3.34, -1.22) * mm});
            skLineSegment(sketch, "E348", {"start": v(-3.34, -1.22) * mm, "end": v(-3.36, -1.22) * mm});
            skLineSegment(sketch, "E349", {"start": v(-3.36, -1.22) * mm, "end": v(-3.37, -1.23) * mm});
            skLineSegment(sketch, "E350", {"start": v(-3.37, -1.23) * mm, "end": v(-3.4, -1.25) * mm});
            skLineSegment(sketch, "E351", {"start": v(-3.4, -1.25) * mm, "end": v(-3.43, -1.26) * mm});
            skLineSegment(sketch, "E352", {"start": v(-3.43, -1.26) * mm, "end": v(-3.46, -1.27) * mm});
            skLineSegment(sketch, "E353", {"start": v(-3.46, -1.27) * mm, "end": v(-3.5, -1.27) * mm});
            skLineSegment(sketch, "E354", {"start": v(-3.5, -1.27) * mm, "end": v(-3.53, -1.28) * mm});
            skLineSegment(sketch, "E355", {"start": v(-3.53, -1.28) * mm, "end": v(-3.57, -1.29) * mm});
            skLineSegment(sketch, "E356", {"start": v(-3.57, -1.29) * mm, "end": v(-3.6, -1.3) * mm});
            skLineSegment(sketch, "E357", {"start": v(-3.6, -1.3) * mm, "end": v(-3.64, -1.3) * mm});
            skLineSegment(sketch, "E358", {"start": v(-3.64, -1.3) * mm, "end": v(-3.68, -1.3) * mm});
            skLineSegment(sketch, "E359", {"start": v(-3.68, -1.3) * mm, "end": v(-3.72, -1.3) * mm});
            skLineSegment(sketch, "E360", {"start": v(-3.72, -1.3) * mm, "end": v(-3.75, -1.3) * mm});
            skLineSegment(sketch, "E361", {"start": v(-3.75, -1.3) * mm, "end": v(-3.78, -1.27) * mm});
            skLineSegment(sketch, "E362", {"start": v(-3.78, -1.27) * mm, "end": v(-3.76, -1.23) * mm});
            skLineSegment(sketch, "E363", {"start": v(-3.76, -1.23) * mm, "end": v(-3.75, -1.2) * mm});
            skLineSegment(sketch, "E364", {"start": v(-3.75, -1.2) * mm, "end": v(-3.74, -1.16) * mm});
            skLineSegment(sketch, "E365", {"start": v(-3.74, -1.16) * mm, "end": v(-3.72, -1.13) * mm});
            skLineSegment(sketch, "E366", {"start": v(-3.72, -1.13) * mm, "end": v(-3.7, -1.1) * mm});
            skLineSegment(sketch, "E367", {"start": v(-3.7, -1.1) * mm, "end": v(-3.7, -1.06) * mm});
            skLineSegment(sketch, "E368", {"start": v(-3.7, -1.06) * mm, "end": v(-3.67, -1.03) * mm});
            skLineSegment(sketch, "E369", {"start": v(-3.67, -1.03) * mm, "end": v(-3.66, -1) * mm});
            skLineSegment(sketch, "E370", {"start": v(-3.66, -1) * mm, "end": v(-3.64, -0.97) * mm});
            skLineSegment(sketch, "E371", {"start": v(-3.64, -0.97) * mm, "end": v(-3.62, -0.94) * mm});
            skLineSegment(sketch, "E372", {"start": v(-3.62, -0.94) * mm, "end": v(-3.6, -0.92) * mm});
            skLineSegment(sketch, "E373", {"start": v(-3.6, -0.92) * mm, "end": v(-3.58, -0.91) * mm});
            skLineSegment(sketch, "E374", {"start": v(-3.58, -0.91) * mm, "end": v(-3.57, -0.9) * mm});
            skLineSegment(sketch, "E375", {"start": v(-3.57, -0.9) * mm, "end": v(-3.56, -0.88) * mm});
            skLineSegment(sketch, "E376", {"start": v(-3.56, -0.88) * mm, "end": v(-3.56, -0.88) * mm});
            skLineSegment(sketch, "E377", {"start": v(-3.56, -0.88) * mm, "end": v(-3.55, -0.87) * mm});
            skLineSegment(sketch, "E378", {"start": v(-3.55, -0.87) * mm, "end": v(-3.55, -0.87) * mm});
            skLineSegment(sketch, "E379", {"start": v(-3.55, -0.87) * mm, "end": v(-3.54, -0.86) * mm});
            skLineSegment(sketch, "E380", {"start": v(-3.54, -0.86) * mm, "end": v(-3.53, -0.86) * mm});
            skLineSegment(sketch, "E381", {"start": v(-3.53, -0.86) * mm, "end": v(-3.53, -0.85) * mm});
            skLineSegment(sketch, "E382", {"start": v(-3.53, -0.85) * mm, "end": v(-3.59, -0.74) * mm});
            skLineSegment(sketch, "E383", {"start": v(-3.59, -0.74) * mm, "end": v(-3.6, -0.74) * mm});
            skLineSegment(sketch, "E384", {"start": v(-3.6, -0.74) * mm, "end": v(-3.6, -0.74) * mm});
            skLineSegment(sketch, "E385", {"start": v(-3.6, -0.74) * mm, "end": v(-3.62, -0.74) * mm});
            skLineSegment(sketch, "E386", {"start": v(-3.62, -0.74) * mm, "end": v(-3.62, -0.74) * mm});
            skLineSegment(sketch, "E387", {"start": v(-3.62, -0.74) * mm, "end": v(-3.63, -0.74) * mm});
            skLineSegment(sketch, "E388", {"start": v(-3.63, -0.74) * mm, "end": v(-3.65, -0.74) * mm});
            skLineSegment(sketch, "E389", {"start": v(-3.65, -0.74) * mm, "end": v(-3.67, -0.74) * mm});
            skLineSegment(sketch, "E390", {"start": v(-3.67, -0.74) * mm, "end": v(-3.68, -0.75) * mm});
            skLineSegment(sketch, "E391", {"start": v(-3.68, -0.75) * mm, "end": v(-3.71, -0.75) * mm});
            skLineSegment(sketch, "E392", {"start": v(-3.71, -0.75) * mm, "end": v(-3.75, -0.75) * mm});
            skLineSegment(sketch, "E393", {"start": v(-3.75, -0.75) * mm, "end": v(-3.78, -0.75) * mm});
            skLineSegment(sketch, "E394", {"start": v(-3.78, -0.75) * mm, "end": v(-3.82, -0.75) * mm});
            skLineSegment(sketch, "E395", {"start": v(-3.82, -0.75) * mm, "end": v(-3.85, -0.74) * mm});
            skLineSegment(sketch, "E396", {"start": v(-3.85, -0.74) * mm, "end": v(-3.89, -0.74) * mm});
            skLineSegment(sketch, "E397", {"start": v(-3.89, -0.74) * mm, "end": v(-3.92, -0.73) * mm});
            skLineSegment(sketch, "E398", {"start": v(-3.92, -0.73) * mm, "end": v(-3.96, -0.72) * mm});
            skLineSegment(sketch, "E399", {"start": v(-3.96, -0.72) * mm, "end": v(-4, -0.71) * mm});
            skLineSegment(sketch, "E400", {"start": v(-4, -0.71) * mm, "end": v(-4.03, -0.7) * mm});
            skLineSegment(sketch, "E401", {"start": v(-4.03, -0.7) * mm, "end": v(-4.07, -0.7) * mm});
            skLineSegment(sketch, "E402", {"start": v(-4.07, -0.7) * mm, "end": v(-4.08, -0.66) * mm});
            skLineSegment(sketch, "E403", {"start": v(-4.08, -0.66) * mm, "end": v(-4.06, -0.62) * mm});
            skLineSegment(sketch, "E404", {"start": v(-4.06, -0.62) * mm, "end": v(-4.03, -0.6) * mm});
            skLineSegment(sketch, "E405", {"start": v(-4.03, -0.6) * mm, "end": v(-4.01, -0.57) * mm});
            skLineSegment(sketch, "E406", {"start": v(-4.01, -0.57) * mm, "end": v(-3.99, -0.54) * mm});
            skLineSegment(sketch, "E407", {"start": v(-3.99, -0.54) * mm, "end": v(-3.96, -0.51) * mm});
            skLineSegment(sketch, "E408", {"start": v(-3.96, -0.51) * mm, "end": v(-3.94, -0.49) * mm});
            skLineSegment(sketch, "E409", {"start": v(-3.94, -0.49) * mm, "end": v(-3.9, -0.46) * mm});
            skLineSegment(sketch, "E410", {"start": v(-3.9, -0.46) * mm, "end": v(-3.88, -0.44) * mm});
            skLineSegment(sketch, "E411", {"start": v(-3.88, -0.44) * mm, "end": v(-3.86, -0.42) * mm});
            skLineSegment(sketch, "E412", {"start": v(-3.86, -0.42) * mm, "end": v(-3.83, -0.4) * mm});
            skLineSegment(sketch, "E413", {"start": v(-3.83, -0.4) * mm, "end": v(-3.8, -0.38) * mm});
            skLineSegment(sketch, "E414", {"start": v(-3.8, -0.38) * mm, "end": v(-3.79, -0.38) * mm});
            skLineSegment(sketch, "E415", {"start": v(-3.79, -0.38) * mm, "end": v(-3.77, -0.37) * mm});
            skLineSegment(sketch, "E416", {"start": v(-3.77, -0.37) * mm, "end": v(-3.76, -0.36) * mm});
            skLineSegment(sketch, "E417", {"start": v(-3.76, -0.36) * mm, "end": v(-3.75, -0.35) * mm});
            skLineSegment(sketch, "E418", {"start": v(-3.75, -0.35) * mm, "end": v(-3.74, -0.35) * mm});
            skLineSegment(sketch, "E419", {"start": v(-3.74, -0.35) * mm, "end": v(-3.74, -0.35) * mm});
            skLineSegment(sketch, "E420", {"start": v(-3.74, -0.35) * mm, "end": v(-3.73, -0.34) * mm});
            skLineSegment(sketch, "E421", {"start": v(-3.73, -0.34) * mm, "end": v(-3.72, -0.34) * mm});
            skLineSegment(sketch, "E422", {"start": v(-3.72, -0.34) * mm, "end": v(-3.71, -0.34) * mm});
            skLineSegment(sketch, "E423", {"start": v(-3.71, -0.34) * mm, "end": v(-3.74, -0.2) * mm});
            skLineSegment(sketch, "E424", {"start": v(-3.74, -0.2) * mm, "end": v(-3.74, -0.2) * mm});
            skLineSegment(sketch, "E425", {"start": v(-3.74, -0.2) * mm, "end": v(-3.75, -0.2) * mm});
            skLineSegment(sketch, "E426", {"start": v(-3.75, -0.2) * mm, "end": v(-3.76, -0.2) * mm});
            skLineSegment(sketch, "E427", {"start": v(-3.76, -0.2) * mm, "end": v(-3.77, -0.2) * mm});
            skLineSegment(sketch, "E428", {"start": v(-3.77, -0.2) * mm, "end": v(-3.77, -0.2) * mm});
            skLineSegment(sketch, "E429", {"start": v(-3.77, -0.2) * mm, "end": v(-3.78, -0.2) * mm});
            skLineSegment(sketch, "E430", {"start": v(-3.78, -0.2) * mm, "end": v(-3.8, -0.2) * mm});
            skLineSegment(sketch, "E431", {"start": v(-3.8, -0.2) * mm, "end": v(-3.82, -0.2) * mm});
            skLineSegment(sketch, "E432", {"start": v(-3.82, -0.2) * mm, "end": v(-3.83, -0.2) * mm});
            skLineSegment(sketch, "E433", {"start": v(-3.83, -0.2) * mm, "end": v(-3.86, -0.19) * mm});
            skLineSegment(sketch, "E434", {"start": v(-3.86, -0.19) * mm, "end": v(-3.9, -0.18) * mm});
            skLineSegment(sketch, "E435", {"start": v(-3.9, -0.18) * mm, "end": v(-3.93, -0.16) * mm});
            skLineSegment(sketch, "E436", {"start": v(-3.93, -0.16) * mm, "end": v(-3.96, -0.15) * mm});
            skLineSegment(sketch, "E437", {"start": v(-3.96, -0.15) * mm, "end": v(-4, -0.14) * mm});
            skLineSegment(sketch, "E438", {"start": v(-4, -0.14) * mm, "end": v(-4.02, -0.12) * mm});
            skLineSegment(sketch, "E439", {"start": v(-4.02, -0.12) * mm, "end": v(-4.06, -0.1) * mm});
            skLineSegment(sketch, "E440", {"start": v(-4.06, -0.1) * mm, "end": v(-4.09, -0.08) * mm});
            skLineSegment(sketch, "E441", {"start": v(-4.09, -0.08) * mm, "end": v(-4.12, -0.06) * mm});
            skLineSegment(sketch, "E442", {"start": v(-4.12, -0.06) * mm, "end": v(-4.15, -0.04) * mm});
            skLineSegment(sketch, "E443", {"start": v(-4.15, -0.04) * mm, "end": v(-4.18, -0.02) * mm});
            skLineSegment(sketch, "E444", {"start": v(-4.18, -0.02) * mm, "end": v(-4.18, 0.02) * mm});
            skLineSegment(sketch, "E445", {"start": v(-4.18, 0.02) * mm, "end": v(-4.15, 0.04) * mm});
            skLineSegment(sketch, "E446", {"start": v(-4.15, 0.04) * mm, "end": v(-4.12, 0.06) * mm});
            skLineSegment(sketch, "E447", {"start": v(-4.12, 0.06) * mm, "end": v(-4.09, 0.08) * mm});
            skLineSegment(sketch, "E448", {"start": v(-4.09, 0.08) * mm, "end": v(-4.06, 0.1) * mm});
            skLineSegment(sketch, "E449", {"start": v(-4.06, 0.1) * mm, "end": v(-4.02, 0.12) * mm});
            skLineSegment(sketch, "E450", {"start": v(-4.02, 0.12) * mm, "end": v(-4, 0.14) * mm});
            skLineSegment(sketch, "E451", {"start": v(-4, 0.14) * mm, "end": v(-3.96, 0.15) * mm});
            skLineSegment(sketch, "E452", {"start": v(-3.96, 0.15) * mm, "end": v(-3.93, 0.16) * mm});
            skLineSegment(sketch, "E453", {"start": v(-3.93, 0.16) * mm, "end": v(-3.9, 0.18) * mm});
            skLineSegment(sketch, "E454", {"start": v(-3.9, 0.18) * mm, "end": v(-3.86, 0.19) * mm});
            skLineSegment(sketch, "E455", {"start": v(-3.86, 0.19) * mm, "end": v(-3.83, 0.2) * mm});
            skLineSegment(sketch, "E456", {"start": v(-3.83, 0.2) * mm, "end": v(-3.82, 0.2) * mm});
            skLineSegment(sketch, "E457", {"start": v(-3.82, 0.2) * mm, "end": v(-3.8, 0.2) * mm});
            skLineSegment(sketch, "E458", {"start": v(-3.8, 0.2) * mm, "end": v(-3.78, 0.2) * mm});
            skLineSegment(sketch, "E459", {"start": v(-3.78, 0.2) * mm, "end": v(-3.77, 0.2) * mm});
            skLineSegment(sketch, "E460", {"start": v(-3.77, 0.2) * mm, "end": v(-3.77, 0.2) * mm});
            skLineSegment(sketch, "E461", {"start": v(-3.77, 0.2) * mm, "end": v(-3.76, 0.2) * mm});
            skLineSegment(sketch, "E462", {"start": v(-3.76, 0.2) * mm, "end": v(-3.75, 0.2) * mm});
            skLineSegment(sketch, "E463", {"start": v(-3.75, 0.2) * mm, "end": v(-3.74, 0.2) * mm});
            skLineSegment(sketch, "E464", {"start": v(-3.74, 0.2) * mm, "end": v(-3.74, 0.2) * mm});
            skLineSegment(sketch, "E465", {"start": v(-3.74, 0.2) * mm, "end": v(-3.71, 0.34) * mm});
            skLineSegment(sketch, "E466", {"start": v(-3.71, 0.34) * mm, "end": v(-3.72, 0.34) * mm});
            skLineSegment(sketch, "E467", {"start": v(-3.72, 0.34) * mm, "end": v(-3.73, 0.34) * mm});
            skLineSegment(sketch, "E468", {"start": v(-3.73, 0.34) * mm, "end": v(-3.74, 0.35) * mm});
            skLineSegment(sketch, "E469", {"start": v(-3.74, 0.35) * mm, "end": v(-3.74, 0.35) * mm});
            skLineSegment(sketch, "E470", {"start": v(-3.74, 0.35) * mm, "end": v(-3.75, 0.35) * mm});
            skLineSegment(sketch, "E471", {"start": v(-3.75, 0.35) * mm, "end": v(-3.76, 0.36) * mm});
            skLineSegment(sketch, "E472", {"start": v(-3.76, 0.36) * mm, "end": v(-3.77, 0.37) * mm});
            skLineSegment(sketch, "E473", {"start": v(-3.77, 0.37) * mm, "end": v(-3.79, 0.38) * mm});
            skLineSegment(sketch, "E474", {"start": v(-3.79, 0.38) * mm, "end": v(-3.8, 0.38) * mm});
            skLineSegment(sketch, "E475", {"start": v(-3.8, 0.38) * mm, "end": v(-3.83, 0.4) * mm});
            skLineSegment(sketch, "E476", {"start": v(-3.83, 0.4) * mm, "end": v(-3.86, 0.42) * mm});
            skLineSegment(sketch, "E477", {"start": v(-3.86, 0.42) * mm, "end": v(-3.88, 0.44) * mm});
            skLineSegment(sketch, "E478", {"start": v(-3.88, 0.44) * mm, "end": v(-3.9, 0.46) * mm});
            skLineSegment(sketch, "E479", {"start": v(-3.9, 0.46) * mm, "end": v(-3.94, 0.49) * mm});
            skLineSegment(sketch, "E480", {"start": v(-3.94, 0.49) * mm, "end": v(-3.96, 0.51) * mm});
            skLineSegment(sketch, "E481", {"start": v(-3.96, 0.51) * mm, "end": v(-3.99, 0.54) * mm});
            skLineSegment(sketch, "E482", {"start": v(-3.99, 0.54) * mm, "end": v(-4.01, 0.57) * mm});
            skLineSegment(sketch, "E483", {"start": v(-4.01, 0.57) * mm, "end": v(-4.03, 0.6) * mm});
            skLineSegment(sketch, "E484", {"start": v(-4.03, 0.6) * mm, "end": v(-4.06, 0.62) * mm});
            skLineSegment(sketch, "E485", {"start": v(-4.06, 0.62) * mm, "end": v(-4.08, 0.66) * mm});
            skLineSegment(sketch, "E486", {"start": v(-4.08, 0.66) * mm, "end": v(-4.07, 0.7) * mm});
            skLineSegment(sketch, "E487", {"start": v(-4.07, 0.7) * mm, "end": v(-4.03, 0.7) * mm});
            skLineSegment(sketch, "E488", {"start": v(-4.03, 0.7) * mm, "end": v(-4, 0.71) * mm});
            skLineSegment(sketch, "E489", {"start": v(-4, 0.71) * mm, "end": v(-3.96, 0.72) * mm});
            skLineSegment(sketch, "E490", {"start": v(-3.96, 0.72) * mm, "end": v(-3.92, 0.73) * mm});
            skLineSegment(sketch, "E491", {"start": v(-3.92, 0.73) * mm, "end": v(-3.89, 0.74) * mm});
            skLineSegment(sketch, "E492", {"start": v(-3.89, 0.74) * mm, "end": v(-3.85, 0.74) * mm});
            skLineSegment(sketch, "E493", {"start": v(-3.85, 0.74) * mm, "end": v(-3.82, 0.75) * mm});
            skLineSegment(sketch, "E494", {"start": v(-3.82, 0.75) * mm, "end": v(-3.78, 0.75) * mm});
            skLineSegment(sketch, "E495", {"start": v(-3.78, 0.75) * mm, "end": v(-3.75, 0.75) * mm});
            skLineSegment(sketch, "E496", {"start": v(-3.75, 0.75) * mm, "end": v(-3.71, 0.75) * mm});
            skLineSegment(sketch, "E497", {"start": v(-3.71, 0.75) * mm, "end": v(-3.68, 0.75) * mm});
            skLineSegment(sketch, "E498", {"start": v(-3.68, 0.75) * mm, "end": v(-3.67, 0.74) * mm});
            skLineSegment(sketch, "E499", {"start": v(-3.67, 0.74) * mm, "end": v(-3.65, 0.74) * mm});
            skLineSegment(sketch, "E500", {"start": v(-3.65, 0.74) * mm, "end": v(-3.63, 0.74) * mm});
            skLineSegment(sketch, "E501", {"start": v(-3.63, 0.74) * mm, "end": v(-3.62, 0.74) * mm});
            skLineSegment(sketch, "E502", {"start": v(-3.62, 0.74) * mm, "end": v(-3.62, 0.74) * mm});
            skLineSegment(sketch, "E503", {"start": v(-3.62, 0.74) * mm, "end": v(-3.6, 0.74) * mm});
            skLineSegment(sketch, "E504", {"start": v(-3.6, 0.74) * mm, "end": v(-3.6, 0.74) * mm});
            skLineSegment(sketch, "E505", {"start": v(-3.6, 0.74) * mm, "end": v(-3.59, 0.74) * mm});
            skLineSegment(sketch, "E506", {"start": v(-3.59, 0.74) * mm, "end": v(-3.53, 0.85) * mm});
            skLineSegment(sketch, "E507", {"start": v(-3.53, 0.85) * mm, "end": v(-3.53, 0.86) * mm});
            skLineSegment(sketch, "E508", {"start": v(-3.53, 0.86) * mm, "end": v(-3.54, 0.86) * mm});
            skLineSegment(sketch, "E509", {"start": v(-3.54, 0.86) * mm, "end": v(-3.55, 0.87) * mm});
            skLineSegment(sketch, "E510", {"start": v(-3.55, 0.87) * mm, "end": v(-3.55, 0.87) * mm});
            skLineSegment(sketch, "E511", {"start": v(-3.55, 0.87) * mm, "end": v(-3.56, 0.88) * mm});
            skLineSegment(sketch, "E512", {"start": v(-3.56, 0.88) * mm, "end": v(-3.56, 0.88) * mm});
            skLineSegment(sketch, "E513", {"start": v(-3.56, 0.88) * mm, "end": v(-3.57, 0.9) * mm});
            skLineSegment(sketch, "E514", {"start": v(-3.57, 0.9) * mm, "end": v(-3.58, 0.91) * mm});
            skLineSegment(sketch, "E515", {"start": v(-3.58, 0.91) * mm, "end": v(-3.6, 0.92) * mm});
            skLineSegment(sketch, "E516", {"start": v(-3.6, 0.92) * mm, "end": v(-3.62, 0.94) * mm});
            skLineSegment(sketch, "E517", {"start": v(-3.62, 0.94) * mm, "end": v(-3.64, 0.97) * mm});
            skLineSegment(sketch, "E518", {"start": v(-3.64, 0.97) * mm, "end": v(-3.66, 1) * mm});
            skLineSegment(sketch, "E519", {"start": v(-3.66, 1) * mm, "end": v(-3.67, 1.03) * mm});
            skLineSegment(sketch, "E520", {"start": v(-3.67, 1.03) * mm, "end": v(-3.7, 1.06) * mm});
            skLineSegment(sketch, "E521", {"start": v(-3.7, 1.06) * mm, "end": v(-3.7, 1.1) * mm});
            skLineSegment(sketch, "E522", {"start": v(-3.7, 1.1) * mm, "end": v(-3.72, 1.13) * mm});
            skLineSegment(sketch, "E523", {"start": v(-3.72, 1.13) * mm, "end": v(-3.74, 1.16) * mm});
            skLineSegment(sketch, "E524", {"start": v(-3.74, 1.16) * mm, "end": v(-3.75, 1.2) * mm});
            skLineSegment(sketch, "E525", {"start": v(-3.75, 1.2) * mm, "end": v(-3.76, 1.23) * mm});
            skLineSegment(sketch, "E526", {"start": v(-3.76, 1.23) * mm, "end": v(-3.78, 1.27) * mm});
            skLineSegment(sketch, "E527", {"start": v(-3.78, 1.27) * mm, "end": v(-3.75, 1.3) * mm});
            skLineSegment(sketch, "E528", {"start": v(-3.75, 1.3) * mm, "end": v(-3.72, 1.3) * mm});
            skLineSegment(sketch, "E529", {"start": v(-3.72, 1.3) * mm, "end": v(-3.68, 1.3) * mm});
            skLineSegment(sketch, "E530", {"start": v(-3.68, 1.3) * mm, "end": v(-3.64, 1.3) * mm});
            skLineSegment(sketch, "E531", {"start": v(-3.64, 1.3) * mm, "end": v(-3.6, 1.3) * mm});
            skLineSegment(sketch, "E532", {"start": v(-3.6, 1.3) * mm, "end": v(-3.57, 1.29) * mm});
            skLineSegment(sketch, "E533", {"start": v(-3.57, 1.29) * mm, "end": v(-3.53, 1.28) * mm});
            skLineSegment(sketch, "E534", {"start": v(-3.53, 1.28) * mm, "end": v(-3.5, 1.27) * mm});
            skLineSegment(sketch, "E535", {"start": v(-3.5, 1.27) * mm, "end": v(-3.46, 1.27) * mm});
            skLineSegment(sketch, "E536", {"start": v(-3.46, 1.27) * mm, "end": v(-3.43, 1.26) * mm});
            skLineSegment(sketch, "E537", {"start": v(-3.43, 1.26) * mm, "end": v(-3.4, 1.25) * mm});
            skLineSegment(sketch, "E538", {"start": v(-3.4, 1.25) * mm, "end": v(-3.37, 1.23) * mm});
            skLineSegment(sketch, "E539", {"start": v(-3.37, 1.23) * mm, "end": v(-3.36, 1.22) * mm});
            skLineSegment(sketch, "E540", {"start": v(-3.36, 1.22) * mm, "end": v(-3.34, 1.22) * mm});
            skLineSegment(sketch, "E541", {"start": v(-3.34, 1.22) * mm, "end": v(-3.32, 1.21) * mm});
            skLineSegment(sketch, "E542", {"start": v(-3.32, 1.21) * mm, "end": v(-3.32, 1.2) * mm});
            skLineSegment(sketch, "E543", {"start": v(-3.32, 1.2) * mm, "end": v(-3.3, 1.2) * mm});
            skLineSegment(sketch, "E544", {"start": v(-3.3, 1.2) * mm, "end": v(-3.3, 1.2) * mm});
            skLineSegment(sketch, "E545", {"start": v(-3.3, 1.2) * mm, "end": v(-3.29, 1.2) * mm});
            skLineSegment(sketch, "E546", {"start": v(-3.29, 1.2) * mm, "end": v(-3.28, 1.19) * mm});
            skLineSegment(sketch, "E547", {"start": v(-3.28, 1.19) * mm, "end": v(-3.19, 1.28) * mm});
            skLineSegment(sketch, "E548", {"start": v(-3.19, 1.28) * mm, "end": v(-3.2, 1.29) * mm});
            skLineSegment(sketch, "E549", {"start": v(-3.2, 1.29) * mm, "end": v(-3.2, 1.3) * mm});
            skLineSegment(sketch, "E550", {"start": v(-3.2, 1.3) * mm, "end": v(-3.2, 1.3) * mm});
            skLineSegment(sketch, "E551", {"start": v(-3.2, 1.3) * mm, "end": v(-3.2, 1.32) * mm});
            skLineSegment(sketch, "E552", {"start": v(-3.2, 1.32) * mm, "end": v(-3.21, 1.32) * mm});
            skLineSegment(sketch, "E553", {"start": v(-3.21, 1.32) * mm, "end": v(-3.22, 1.34) * mm});
            skLineSegment(sketch, "E554", {"start": v(-3.22, 1.34) * mm, "end": v(-3.22, 1.36) * mm});
            skLineSegment(sketch, "E555", {"start": v(-3.22, 1.36) * mm, "end": v(-3.23, 1.37) * mm});
            skLineSegment(sketch, "E556", {"start": v(-3.23, 1.37) * mm, "end": v(-3.25, 1.4) * mm});
            skLineSegment(sketch, "E557", {"start": v(-3.25, 1.4) * mm, "end": v(-3.26, 1.43) * mm});
            skLineSegment(sketch, "E558", {"start": v(-3.26, 1.43) * mm, "end": v(-3.27, 1.46) * mm});
            skLineSegment(sketch, "E559", {"start": v(-3.27, 1.46) * mm, "end": v(-3.27, 1.5) * mm});
            skLineSegment(sketch, "E560", {"start": v(-3.27, 1.5) * mm, "end": v(-3.28, 1.53) * mm});
            skLineSegment(sketch, "E561", {"start": v(-3.28, 1.53) * mm, "end": v(-3.29, 1.57) * mm});
            skLineSegment(sketch, "E562", {"start": v(-3.29, 1.57) * mm, "end": v(-3.3, 1.6) * mm});
            skLineSegment(sketch, "E563", {"start": v(-3.3, 1.6) * mm, "end": v(-3.3, 1.64) * mm});
            skLineSegment(sketch, "E564", {"start": v(-3.3, 1.64) * mm, "end": v(-3.3, 1.68) * mm});
            skLineSegment(sketch, "E565", {"start": v(-3.3, 1.68) * mm, "end": v(-3.3, 1.72) * mm});
            skLineSegment(sketch, "E566", {"start": v(-3.3, 1.72) * mm, "end": v(-3.3, 1.75) * mm});
            skLineSegment(sketch, "E567", {"start": v(-3.3, 1.75) * mm, "end": v(-3.27, 1.78) * mm});
            skLineSegment(sketch, "E568", {"start": v(-3.27, 1.78) * mm, "end": v(-3.23, 1.76) * mm});
            skLineSegment(sketch, "E569", {"start": v(-3.23, 1.76) * mm, "end": v(-3.2, 1.75) * mm});
            skLineSegment(sketch, "E570", {"start": v(-3.2, 1.75) * mm, "end": v(-3.16, 1.74) * mm});
            skLineSegment(sketch, "E571", {"start": v(-3.16, 1.74) * mm, "end": v(-3.13, 1.72) * mm});
            skLineSegment(sketch, "E572", {"start": v(-3.13, 1.72) * mm, "end": v(-3.1, 1.7) * mm});
            skLineSegment(sketch, "E573", {"start": v(-3.1, 1.7) * mm, "end": v(-3.06, 1.7) * mm});
            skLineSegment(sketch, "E574", {"start": v(-3.06, 1.7) * mm, "end": v(-3.03, 1.67) * mm});
            skLineSegment(sketch, "E575", {"start": v(-3.03, 1.67) * mm, "end": v(-3, 1.66) * mm});
            skLineSegment(sketch, "E576", {"start": v(-3, 1.66) * mm, "end": v(-2.97, 1.64) * mm});
            skLineSegment(sketch, "E577", {"start": v(-2.97, 1.64) * mm, "end": v(-2.94, 1.62) * mm});
            skLineSegment(sketch, "E578", {"start": v(-2.94, 1.62) * mm, "end": v(-2.92, 1.6) * mm});
            skLineSegment(sketch, "E579", {"start": v(-2.92, 1.6) * mm, "end": v(-2.91, 1.58) * mm});
            skLineSegment(sketch, "E580", {"start": v(-2.91, 1.58) * mm, "end": v(-2.9, 1.57) * mm});
            skLineSegment(sketch, "E581", {"start": v(-2.9, 1.57) * mm, "end": v(-2.88, 1.56) * mm});
            skLineSegment(sketch, "E582", {"start": v(-2.88, 1.56) * mm, "end": v(-2.88, 1.56) * mm});
            skLineSegment(sketch, "E583", {"start": v(-2.88, 1.56) * mm, "end": v(-2.87, 1.55) * mm});
            skLineSegment(sketch, "E584", {"start": v(-2.87, 1.55) * mm, "end": v(-2.87, 1.55) * mm});
            skLineSegment(sketch, "E585", {"start": v(-2.87, 1.55) * mm, "end": v(-2.86, 1.54) * mm});
            skLineSegment(sketch, "E586", {"start": v(-2.86, 1.54) * mm, "end": v(-2.86, 1.53) * mm});
            skLineSegment(sketch, "E587", {"start": v(-2.86, 1.53) * mm, "end": v(-2.85, 1.53) * mm});
            skLineSegment(sketch, "E588", {"start": v(-2.85, 1.53) * mm, "end": v(-2.74, 1.59) * mm});
            skLineSegment(sketch, "E589", {"start": v(-2.74, 1.59) * mm, "end": v(-2.74, 1.6) * mm});
            skLineSegment(sketch, "E590", {"start": v(-2.74, 1.6) * mm, "end": v(-2.74, 1.6) * mm});
            skLineSegment(sketch, "E591", {"start": v(-2.74, 1.6) * mm, "end": v(-2.74, 1.62) * mm});
            skLineSegment(sketch, "E592", {"start": v(-2.74, 1.62) * mm, "end": v(-2.74, 1.62) * mm});
            skLineSegment(sketch, "E593", {"start": v(-2.74, 1.62) * mm, "end": v(-2.74, 1.63) * mm});
            skLineSegment(sketch, "E594", {"start": v(-2.74, 1.63) * mm, "end": v(-2.74, 1.65) * mm});
            skLineSegment(sketch, "E595", {"start": v(-2.74, 1.65) * mm, "end": v(-2.74, 1.67) * mm});
            skLineSegment(sketch, "E596", {"start": v(-2.74, 1.67) * mm, "end": v(-2.75, 1.68) * mm});
            skLineSegment(sketch, "E597", {"start": v(-2.75, 1.68) * mm, "end": v(-2.75, 1.71) * mm});
            skLineSegment(sketch, "E598", {"start": v(-2.75, 1.71) * mm, "end": v(-2.75, 1.75) * mm});
            skLineSegment(sketch, "E599", {"start": v(-2.75, 1.75) * mm, "end": v(-2.75, 1.78) * mm});
            skLineSegment(sketch, "E600", {"start": v(-2.75, 1.78) * mm, "end": v(-2.75, 1.82) * mm});
            skLineSegment(sketch, "E601", {"start": v(-2.75, 1.82) * mm, "end": v(-2.74, 1.85) * mm});
            skLineSegment(sketch, "E602", {"start": v(-2.74, 1.85) * mm, "end": v(-2.74, 1.89) * mm});
            skLineSegment(sketch, "E603", {"start": v(-2.74, 1.89) * mm, "end": v(-2.73, 1.92) * mm});
            skLineSegment(sketch, "E604", {"start": v(-2.73, 1.92) * mm, "end": v(-2.72, 1.96) * mm});
            skLineSegment(sketch, "E605", {"start": v(-2.72, 1.96) * mm, "end": v(-2.71, 2) * mm});
            skLineSegment(sketch, "E606", {"start": v(-2.71, 2) * mm, "end": v(-2.7, 2.03) * mm});
            skLineSegment(sketch, "E607", {"start": v(-2.7, 2.03) * mm, "end": v(-2.7, 2.07) * mm});
            skLineSegment(sketch, "E608", {"start": v(-2.7, 2.07) * mm, "end": v(-2.66, 2.08) * mm});
            skLineSegment(sketch, "E609", {"start": v(-2.66, 2.08) * mm, "end": v(-2.62, 2.06) * mm});
            skLineSegment(sketch, "E610", {"start": v(-2.62, 2.06) * mm, "end": v(-2.6, 2.03) * mm});
            skLineSegment(sketch, "E611", {"start": v(-2.6, 2.03) * mm, "end": v(-2.57, 2.01) * mm});
            skLineSegment(sketch, "E612", {"start": v(-2.57, 2.01) * mm, "end": v(-2.54, 1.99) * mm});
            skLineSegment(sketch, "E613", {"start": v(-2.54, 1.99) * mm, "end": v(-2.51, 1.96) * mm});
            skLineSegment(sketch, "E614", {"start": v(-2.51, 1.96) * mm, "end": v(-2.49, 1.94) * mm});
            skLineSegment(sketch, "E615", {"start": v(-2.49, 1.94) * mm, "end": v(-2.46, 1.9) * mm});
            skLineSegment(sketch, "E616", {"start": v(-2.46, 1.9) * mm, "end": v(-2.44, 1.88) * mm});
            skLineSegment(sketch, "E617", {"start": v(-2.44, 1.88) * mm, "end": v(-2.42, 1.86) * mm});
            skLineSegment(sketch, "E618", {"start": v(-2.42, 1.86) * mm, "end": v(-2.4, 1.83) * mm});
            skLineSegment(sketch, "E619", {"start": v(-2.4, 1.83) * mm, "end": v(-2.38, 1.8) * mm});
            skLineSegment(sketch, "E620", {"start": v(-2.38, 1.8) * mm, "end": v(-2.38, 1.79) * mm});
            skLineSegment(sketch, "E621", {"start": v(-2.38, 1.79) * mm, "end": v(-2.37, 1.77) * mm});
            skLineSegment(sketch, "E622", {"start": v(-2.37, 1.77) * mm, "end": v(-2.36, 1.76) * mm});
            skLineSegment(sketch, "E623", {"start": v(-2.36, 1.76) * mm, "end": v(-2.35, 1.75) * mm});
            skLineSegment(sketch, "E624", {"start": v(-2.35, 1.75) * mm, "end": v(-2.35, 1.74) * mm});
            skLineSegment(sketch, "E625", {"start": v(-2.35, 1.74) * mm, "end": v(-2.35, 1.74) * mm});
            skLineSegment(sketch, "E626", {"start": v(-2.35, 1.74) * mm, "end": v(-2.34, 1.73) * mm});
            skLineSegment(sketch, "E627", {"start": v(-2.34, 1.73) * mm, "end": v(-2.34, 1.72) * mm});
            skLineSegment(sketch, "E628", {"start": v(-2.34, 1.72) * mm, "end": v(-2.34, 1.71) * mm});
            skLineSegment(sketch, "E629", {"start": v(-2.34, 1.71) * mm, "end": v(-2.2, 1.74) * mm});
            skLineSegment(sketch, "E630", {"start": v(-2.2, 1.74) * mm, "end": v(-2.2, 1.74) * mm});
            skLineSegment(sketch, "E631", {"start": v(-2.2, 1.74) * mm, "end": v(-2.2, 1.75) * mm});
            skLineSegment(sketch, "E632", {"start": v(-2.2, 1.75) * mm, "end": v(-2.2, 1.76) * mm});
            skLineSegment(sketch, "E633", {"start": v(-2.2, 1.76) * mm, "end": v(-2.2, 1.77) * mm});
            skLineSegment(sketch, "E634", {"start": v(-2.2, 1.77) * mm, "end": v(-2.2, 1.77) * mm});
            skLineSegment(sketch, "E635", {"start": v(-2.2, 1.77) * mm, "end": v(-2.2, 1.78) * mm});
            skLineSegment(sketch, "E636", {"start": v(-2.2, 1.78) * mm, "end": v(-2.2, 1.8) * mm});
            skLineSegment(sketch, "E637", {"start": v(-2.2, 1.8) * mm, "end": v(-2.2, 1.82) * mm});
            skLineSegment(sketch, "E638", {"start": v(-2.2, 1.82) * mm, "end": v(-2.2, 1.83) * mm});
            skLineSegment(sketch, "E639", {"start": v(-2.2, 1.83) * mm, "end": v(-2.19, 1.86) * mm});
            skLineSegment(sketch, "E640", {"start": v(-2.19, 1.86) * mm, "end": v(-2.18, 1.9) * mm});
            skLineSegment(sketch, "E641", {"start": v(-2.18, 1.9) * mm, "end": v(-2.16, 1.93) * mm});
            skLineSegment(sketch, "E642", {"start": v(-2.16, 1.93) * mm, "end": v(-2.15, 1.96) * mm});
            skLineSegment(sketch, "E643", {"start": v(-2.15, 1.96) * mm, "end": v(-2.14, 2) * mm});
            skLineSegment(sketch, "E644", {"start": v(-2.14, 2) * mm, "end": v(-2.12, 2.02) * mm});
            skLineSegment(sketch, "E645", {"start": v(-2.12, 2.02) * mm, "end": v(-2.1, 2.06) * mm});
            skLineSegment(sketch, "E646", {"start": v(-2.1, 2.06) * mm, "end": v(-2.08, 2.09) * mm});
            skLineSegment(sketch, "E647", {"start": v(-2.08, 2.09) * mm, "end": v(-2.06, 2.12) * mm});
            skLineSegment(sketch, "E648", {"start": v(-2.06, 2.12) * mm, "end": v(-2.04, 2.15) * mm});
            skLineSegment(sketch, "E649", {"start": v(-2.04, 2.15) * mm, "end": v(-2.02, 2.18) * mm});
            skLineSegment(sketch, "E650", {"start": v(-2.02, 2.18) * mm, "end": v(-1.98, 2.18) * mm});
            skLineSegment(sketch, "E651", {"start": v(-1.98, 2.18) * mm, "end": v(-1.96, 2.15) * mm});
            skLineSegment(sketch, "E652", {"start": v(-1.96, 2.15) * mm, "end": v(-1.94, 2.12) * mm});
            skLineSegment(sketch, "E653", {"start": v(-1.94, 2.12) * mm, "end": v(-1.92, 2.09) * mm});
            skLineSegment(sketch, "E654", {"start": v(-1.92, 2.09) * mm, "end": v(-1.9, 2.06) * mm});
            skLineSegment(sketch, "E655", {"start": v(-1.9, 2.06) * mm, "end": v(-1.88, 2.02) * mm});
            skLineSegment(sketch, "E656", {"start": v(-1.88, 2.02) * mm, "end": v(-1.86, 2) * mm});
            skLineSegment(sketch, "E657", {"start": v(-1.86, 2) * mm, "end": v(-1.85, 1.96) * mm});
            skLineSegment(sketch, "E658", {"start": v(-1.85, 1.96) * mm, "end": v(-1.84, 1.93) * mm});
            skLineSegment(sketch, "E659", {"start": v(-1.84, 1.93) * mm, "end": v(-1.82, 1.9) * mm});
            skLineSegment(sketch, "E660", {"start": v(-1.82, 1.9) * mm, "end": v(-1.81, 1.86) * mm});
            skLineSegment(sketch, "E661", {"start": v(-1.81, 1.86) * mm, "end": v(-1.8, 1.83) * mm});
            skLineSegment(sketch, "E662", {"start": v(-1.8, 1.83) * mm, "end": v(-1.8, 1.82) * mm});
            skLineSegment(sketch, "E663", {"start": v(-1.8, 1.82) * mm, "end": v(-1.8, 1.8) * mm});
            skLineSegment(sketch, "E664", {"start": v(-1.8, 1.8) * mm, "end": v(-1.8, 1.78) * mm});
            skLineSegment(sketch, "E665", {"start": v(-1.8, 1.78) * mm, "end": v(-1.8, 1.77) * mm});
            skLineSegment(sketch, "E666", {"start": v(-1.8, 1.77) * mm, "end": v(-1.8, 1.77) * mm});
            skLineSegment(sketch, "E667", {"start": v(-1.8, 1.77) * mm, "end": v(-1.8, 1.76) * mm});
            skLineSegment(sketch, "E668", {"start": v(-1.8, 1.76) * mm, "end": v(-1.8, 1.75) * mm});
            skLineSegment(sketch, "E669", {"start": v(-1.8, 1.75) * mm, "end": v(-1.8, 1.74) * mm});
            skLineSegment(sketch, "E670", {"start": v(-1.8, 1.74) * mm, "end": v(-1.8, 1.74) * mm});
            skLineSegment(sketch, "E671", {"start": v(-1.8, 1.74) * mm, "end": v(-1.66, 1.71) * mm});
            skLineSegment(sketch, "E672", {"start": v(-1.66, 1.71) * mm, "end": v(-1.66, 1.72) * mm});
            skLineSegment(sketch, "E673", {"start": v(-1.66, 1.72) * mm, "end": v(-1.66, 1.73) * mm});
            skLineSegment(sketch, "E674", {"start": v(-1.66, 1.73) * mm, "end": v(-1.65, 1.74) * mm});
            skLineSegment(sketch, "E675", {"start": v(-1.65, 1.74) * mm, "end": v(-1.65, 1.74) * mm});
            skLineSegment(sketch, "E676", {"start": v(-1.65, 1.74) * mm, "end": v(-1.65, 1.75) * mm});
            skLineSegment(sketch, "E677", {"start": v(-1.65, 1.75) * mm, "end": v(-1.64, 1.76) * mm});
            skLineSegment(sketch, "E678", {"start": v(-1.64, 1.76) * mm, "end": v(-1.63, 1.77) * mm});
            skLineSegment(sketch, "E679", {"start": v(-1.63, 1.77) * mm, "end": v(-1.62, 1.79) * mm});
            skLineSegment(sketch, "E680", {"start": v(-1.62, 1.79) * mm, "end": v(-1.62, 1.8) * mm});
            skLineSegment(sketch, "E681", {"start": v(-1.62, 1.8) * mm, "end": v(-1.6, 1.83) * mm});
            skLineSegment(sketch, "E682", {"start": v(-1.6, 1.83) * mm, "end": v(-1.58, 1.86) * mm});
            skLineSegment(sketch, "E683", {"start": v(-1.58, 1.86) * mm, "end": v(-1.56, 1.88) * mm});
            skLineSegment(sketch, "E684", {"start": v(-1.56, 1.88) * mm, "end": v(-1.54, 1.9) * mm});
            skLineSegment(sketch, "E685", {"start": v(-1.54, 1.9) * mm, "end": v(-1.51, 1.94) * mm});
            skLineSegment(sketch, "E686", {"start": v(-1.51, 1.94) * mm, "end": v(-1.49, 1.96) * mm});
            skLineSegment(sketch, "E687", {"start": v(-1.49, 1.96) * mm, "end": v(-1.46, 1.99) * mm});
            skLineSegment(sketch, "E688", {"start": v(-1.46, 1.99) * mm, "end": v(-1.43, 2.01) * mm});
            skLineSegment(sketch, "E689", {"start": v(-1.43, 2.01) * mm, "end": v(-1.4, 2.03) * mm});
            skLineSegment(sketch, "E690", {"start": v(-1.4, 2.03) * mm, "end": v(-1.38, 2.06) * mm});
            skLineSegment(sketch, "E691", {"start": v(-1.38, 2.06) * mm, "end": v(-1.34, 2.08) * mm});
            skLineSegment(sketch, "E692", {"start": v(-1.34, 2.08) * mm, "end": v(-1.3, 2.07) * mm});
            skLineSegment(sketch, "E693", {"start": v(-1.3, 2.07) * mm, "end": v(-1.3, 2.03) * mm});
            skLineSegment(sketch, "E694", {"start": v(-1.3, 2.03) * mm, "end": v(-1.29, 2) * mm});
            skLineSegment(sketch, "E695", {"start": v(-1.29, 2) * mm, "end": v(-1.28, 1.96) * mm});
            skLineSegment(sketch, "E696", {"start": v(-1.28, 1.96) * mm, "end": v(-1.27, 1.92) * mm});
            skLineSegment(sketch, "E697", {"start": v(-1.27, 1.92) * mm, "end": v(-1.26, 1.89) * mm});
            skLineSegment(sketch, "E698", {"start": v(-1.26, 1.89) * mm, "end": v(-1.26, 1.85) * mm});
            skLineSegment(sketch, "E699", {"start": v(-1.26, 1.85) * mm, "end": v(-1.25, 1.82) * mm});
            skLineSegment(sketch, "E700", {"start": v(-1.25, 1.82) * mm, "end": v(-1.25, 1.78) * mm});
            skLineSegment(sketch, "E701", {"start": v(-1.25, 1.78) * mm, "end": v(-1.25, 1.75) * mm});
            skLineSegment(sketch, "E702", {"start": v(-1.25, 1.75) * mm, "end": v(-1.25, 1.71) * mm});
            skLineSegment(sketch, "E703", {"start": v(-1.25, 1.71) * mm, "end": v(-1.25, 1.68) * mm});
            skLineSegment(sketch, "E704", {"start": v(-1.25, 1.68) * mm, "end": v(-1.26, 1.67) * mm});
            skLineSegment(sketch, "E705", {"start": v(-1.26, 1.67) * mm, "end": v(-1.26, 1.65) * mm});
            skLineSegment(sketch, "E706", {"start": v(-1.26, 1.65) * mm, "end": v(-1.26, 1.63) * mm});
            skLineSegment(sketch, "E707", {"start": v(-1.26, 1.63) * mm, "end": v(-1.26, 1.62) * mm});
            skLineSegment(sketch, "E708", {"start": v(-1.26, 1.62) * mm, "end": v(-1.26, 1.62) * mm});
            skLineSegment(sketch, "E709", {"start": v(-1.26, 1.62) * mm, "end": v(-1.26, 1.6) * mm});
            skLineSegment(sketch, "E710", {"start": v(-1.26, 1.6) * mm, "end": v(-1.26, 1.6) * mm});
            skLineSegment(sketch, "E711", {"start": v(-1.26, 1.6) * mm, "end": v(-1.26, 1.59) * mm});
            skLineSegment(sketch, "E712", {"start": v(-1.26, 1.59) * mm, "end": v(-1.15, 1.53) * mm});
            skLineSegment(sketch, "E713", {"start": v(-1.15, 1.53) * mm, "end": v(-1.14, 1.53) * mm});
            skLineSegment(sketch, "E714", {"start": v(-1.14, 1.53) * mm, "end": v(-1.14, 1.54) * mm});
            skLineSegment(sketch, "E715", {"start": v(-1.14, 1.54) * mm, "end": v(-1.13, 1.55) * mm});
            skLineSegment(sketch, "E716", {"start": v(-1.13, 1.55) * mm, "end": v(-1.13, 1.55) * mm});
            skLineSegment(sketch, "E717", {"start": v(-1.13, 1.55) * mm, "end": v(-1.12, 1.56) * mm});
            skLineSegment(sketch, "E718", {"start": v(-1.12, 1.56) * mm, "end": v(-1.12, 1.56) * mm});
            skLineSegment(sketch, "E719", {"start": v(-1.12, 1.56) * mm, "end": v(-1.1, 1.57) * mm});
            skLineSegment(sketch, "E720", {"start": v(-1.1, 1.57) * mm, "end": v(-1.09, 1.58) * mm});
            skLineSegment(sketch, "E721", {"start": v(-1.09, 1.58) * mm, "end": v(-1.08, 1.6) * mm});
            skLineSegment(sketch, "E722", {"start": v(-1.08, 1.6) * mm, "end": v(-1.06, 1.62) * mm});
            skLineSegment(sketch, "E723", {"start": v(-1.06, 1.62) * mm, "end": v(-1.03, 1.64) * mm});
            skLineSegment(sketch, "E724", {"start": v(-1.03, 1.64) * mm, "end": v(-1, 1.66) * mm});
            skLineSegment(sketch, "E725", {"start": v(-1, 1.66) * mm, "end": v(-0.97, 1.67) * mm});
            skLineSegment(sketch, "E726", {"start": v(-0.97, 1.67) * mm, "end": v(-0.94, 1.7) * mm});
            skLineSegment(sketch, "E727", {"start": v(-0.94, 1.7) * mm, "end": v(-0.9, 1.7) * mm});
            skLineSegment(sketch, "E728", {"start": v(-0.9, 1.7) * mm, "end": v(-0.87, 1.72) * mm});
            skLineSegment(sketch, "E729", {"start": v(-0.87, 1.72) * mm, "end": v(-0.84, 1.74) * mm});
            skLineSegment(sketch, "E730", {"start": v(-0.84, 1.74) * mm, "end": v(-0.8, 1.75) * mm});
            skLineSegment(sketch, "E731", {"start": v(-0.8, 1.75) * mm, "end": v(-0.77, 1.76) * mm});
            skLineSegment(sketch, "E732", {"start": v(-0.77, 1.76) * mm, "end": v(-0.73, 1.78) * mm});
            skLineSegment(sketch, "E733", {"start": v(-0.73, 1.78) * mm, "end": v(-0.7, 1.75) * mm});
            skLineSegment(sketch, "E734", {"start": v(-0.7, 1.75) * mm, "end": v(-0.7, 1.72) * mm});
            skLineSegment(sketch, "E735", {"start": v(-0.7, 1.72) * mm, "end": v(-0.7, 1.68) * mm});
            skLineSegment(sketch, "E736", {"start": v(-0.7, 1.68) * mm, "end": v(-0.7, 1.64) * mm});
            skLineSegment(sketch, "E737", {"start": v(-0.7, 1.64) * mm, "end": v(-0.7, 1.6) * mm});
            skLineSegment(sketch, "E738", {"start": v(-0.7, 1.6) * mm, "end": v(-0.71, 1.57) * mm});
            skLineSegment(sketch, "E739", {"start": v(-0.71, 1.57) * mm, "end": v(-0.72, 1.53) * mm});
            skLineSegment(sketch, "E740", {"start": v(-0.72, 1.53) * mm, "end": v(-0.73, 1.5) * mm});
            skLineSegment(sketch, "E741", {"start": v(-0.73, 1.5) * mm, "end": v(-0.73, 1.46) * mm});
            skLineSegment(sketch, "E742", {"start": v(-0.73, 1.46) * mm, "end": v(-0.74, 1.43) * mm});
            skLineSegment(sketch, "E743", {"start": v(-0.74, 1.43) * mm, "end": v(-0.75, 1.4) * mm});
            skLineSegment(sketch, "E744", {"start": v(-0.75, 1.4) * mm, "end": v(-0.77, 1.37) * mm});
            skLineSegment(sketch, "E745", {"start": v(-0.77, 1.37) * mm, "end": v(-0.78, 1.36) * mm});
            skLineSegment(sketch, "E746", {"start": v(-0.78, 1.36) * mm, "end": v(-0.78, 1.34) * mm});
            skLineSegment(sketch, "E747", {"start": v(-0.78, 1.34) * mm, "end": v(-0.79, 1.32) * mm});
            skLineSegment(sketch, "E748", {"start": v(-0.79, 1.32) * mm, "end": v(-0.8, 1.32) * mm});
            skLineSegment(sketch, "E749", {"start": v(-0.8, 1.32) * mm, "end": v(-0.8, 1.3) * mm});
            skLineSegment(sketch, "E750", {"start": v(-0.8, 1.3) * mm, "end": v(-0.8, 1.3) * mm});
            skLineSegment(sketch, "E751", {"start": v(-0.8, 1.3) * mm, "end": v(-0.8, 1.29) * mm});
            skLineSegment(sketch, "E752", {"start": v(-0.8, 1.29) * mm, "end": v(-0.81, 1.28) * mm});
            skLineSegment(sketch, "E753", {"start": v(-0.81, 1.28) * mm, "end": v(-0.72, 1.19) * mm});
            skLineSegment(sketch, "E754", {"start": v(-0.72, 1.19) * mm, "end": v(-0.71, 1.2) * mm});
            skLineSegment(sketch, "E755", {"start": v(-0.71, 1.2) * mm, "end": v(-0.7, 1.2) * mm});
            skLineSegment(sketch, "E756", {"start": v(-0.7, 1.2) * mm, "end": v(-0.7, 1.2) * mm});
            skLineSegment(sketch, "E757", {"start": v(-0.7, 1.2) * mm, "end": v(-0.68, 1.2) * mm});
            skLineSegment(sketch, "E758", {"start": v(-0.68, 1.2) * mm, "end": v(-0.68, 1.21) * mm});
            skLineSegment(sketch, "E759", {"start": v(-0.68, 1.21) * mm, "end": v(-0.66, 1.22) * mm});
            skLineSegment(sketch, "E760", {"start": v(-0.66, 1.22) * mm, "end": v(-0.64, 1.22) * mm});
            skLineSegment(sketch, "E761", {"start": v(-0.64, 1.22) * mm, "end": v(-0.63, 1.23) * mm});
            skLineSegment(sketch, "E762", {"start": v(-0.63, 1.23) * mm, "end": v(-0.6, 1.25) * mm});
            skLineSegment(sketch, "E763", {"start": v(-0.6, 1.25) * mm, "end": v(-0.57, 1.26) * mm});
            skLineSegment(sketch, "E764", {"start": v(-0.57, 1.26) * mm, "end": v(-0.54, 1.27) * mm});
            skLineSegment(sketch, "E765", {"start": v(-0.54, 1.27) * mm, "end": v(-0.5, 1.27) * mm});
            skLineSegment(sketch, "E766", {"start": v(-0.5, 1.27) * mm, "end": v(-0.47, 1.28) * mm});
            skLineSegment(sketch, "E767", {"start": v(-0.47, 1.28) * mm, "end": v(-0.43, 1.29) * mm});
            skLineSegment(sketch, "E768", {"start": v(-0.43, 1.29) * mm, "end": v(-0.4, 1.3) * mm});
            skLineSegment(sketch, "E769", {"start": v(-0.4, 1.3) * mm, "end": v(-0.36, 1.3) * mm});
            skLineSegment(sketch, "E770", {"start": v(-0.36, 1.3) * mm, "end": v(-0.32, 1.3) * mm});
            skLineSegment(sketch, "E771", {"start": v(-0.32, 1.3) * mm, "end": v(-0.28, 1.3) * mm});
            skLineSegment(sketch, "E772", {"start": v(-0.28, 1.3) * mm, "end": v(-0.25, 1.3) * mm});
            skLineSegment(sketch, "E773", {"start": v(-0.25, 1.3) * mm, "end": v(-0.22, 1.27) * mm});
            skLineSegment(sketch, "E774", {"start": v(-0.22, 1.27) * mm, "end": v(-0.24, 1.23) * mm});
            skLineSegment(sketch, "E775", {"start": v(-0.24, 1.23) * mm, "end": v(-0.25, 1.2) * mm});
            skLineSegment(sketch, "E776", {"start": v(-0.25, 1.2) * mm, "end": v(-0.26, 1.16) * mm});
            skLineSegment(sketch, "E777", {"start": v(-0.26, 1.16) * mm, "end": v(-0.28, 1.13) * mm});
            skLineSegment(sketch, "E778", {"start": v(-0.28, 1.13) * mm, "end": v(-0.3, 1.1) * mm});
            skLineSegment(sketch, "E779", {"start": v(-0.3, 1.1) * mm, "end": v(-0.3, 1.06) * mm});
            skLineSegment(sketch, "E780", {"start": v(-0.3, 1.06) * mm, "end": v(-0.33, 1.03) * mm});
            skLineSegment(sketch, "E781", {"start": v(-0.33, 1.03) * mm, "end": v(-0.34, 1) * mm});
            skLineSegment(sketch, "E782", {"start": v(-0.34, 1) * mm, "end": v(-0.36, 0.97) * mm});
            skLineSegment(sketch, "E783", {"start": v(-0.36, 0.97) * mm, "end": v(-0.38, 0.94) * mm});
            skLineSegment(sketch, "E784", {"start": v(-0.38, 0.94) * mm, "end": v(-0.4, 0.92) * mm});
            skLineSegment(sketch, "E785", {"start": v(-0.4, 0.92) * mm, "end": v(-0.42, 0.91) * mm});
            skLineSegment(sketch, "E786", {"start": v(-0.42, 0.91) * mm, "end": v(-0.43, 0.9) * mm});
            skLineSegment(sketch, "E787", {"start": v(-0.43, 0.9) * mm, "end": v(-0.44, 0.88) * mm});
            skLineSegment(sketch, "E788", {"start": v(-0.44, 0.88) * mm, "end": v(-0.44, 0.88) * mm});
            skLineSegment(sketch, "E789", {"start": v(-0.44, 0.88) * mm, "end": v(-0.45, 0.87) * mm});
            skLineSegment(sketch, "E790", {"start": v(-0.45, 0.87) * mm, "end": v(-0.45, 0.87) * mm});
            skLineSegment(sketch, "E791", {"start": v(-0.45, 0.87) * mm, "end": v(-0.46, 0.86) * mm});
            skLineSegment(sketch, "E792", {"start": v(-0.46, 0.86) * mm, "end": v(-0.47, 0.86) * mm});
            skLineSegment(sketch, "E793", {"start": v(-0.47, 0.86) * mm, "end": v(-0.47, 0.85) * mm});
            skLineSegment(sketch, "E794", {"start": v(-0.47, 0.85) * mm, "end": v(-0.41, 0.74) * mm});
            skLineSegment(sketch, "E795", {"start": v(-0.41, 0.74) * mm, "end": v(-0.4, 0.74) * mm});
            skLineSegment(sketch, "E796", {"start": v(-0.4, 0.74) * mm, "end": v(-0.4, 0.74) * mm});
            skLineSegment(sketch, "E797", {"start": v(-0.4, 0.74) * mm, "end": v(-0.38, 0.74) * mm});
            skLineSegment(sketch, "E798", {"start": v(-0.38, 0.74) * mm, "end": v(-0.38, 0.74) * mm});
            skLineSegment(sketch, "E799", {"start": v(-0.38, 0.74) * mm, "end": v(-0.37, 0.74) * mm});
            skLineSegment(sketch, "E800", {"start": v(-0.37, 0.74) * mm, "end": v(-0.35, 0.74) * mm});
            skLineSegment(sketch, "E801", {"start": v(-0.35, 0.74) * mm, "end": v(-0.33, 0.74) * mm});
            skLineSegment(sketch, "E802", {"start": v(-0.33, 0.74) * mm, "end": v(-0.32, 0.75) * mm});
            skLineSegment(sketch, "E803", {"start": v(-0.32, 0.75) * mm, "end": v(-0.29, 0.75) * mm});
            skLineSegment(sketch, "E804", {"start": v(-0.29, 0.75) * mm, "end": v(-0.25, 0.75) * mm});
            skLineSegment(sketch, "E805", {"start": v(-0.25, 0.75) * mm, "end": v(-0.22, 0.75) * mm});
            skLineSegment(sketch, "E806", {"start": v(-0.22, 0.75) * mm, "end": v(-0.18, 0.75) * mm});
            skLineSegment(sketch, "E807", {"start": v(-0.18, 0.75) * mm, "end": v(-0.15, 0.74) * mm});
            skLineSegment(sketch, "E808", {"start": v(-0.15, 0.74) * mm, "end": v(-0.11, 0.74) * mm});
            skLineSegment(sketch, "E809", {"start": v(-0.11, 0.74) * mm, "end": v(-0.08, 0.73) * mm});
            skLineSegment(sketch, "E810", {"start": v(-0.08, 0.73) * mm, "end": v(-0.04, 0.72) * mm});
            skLineSegment(sketch, "E811", {"start": v(-0.04, 0.72) * mm, "end": v(0, 0.71) * mm});
            skLineSegment(sketch, "E812", {"start": v(0, 0.71) * mm, "end": v(0.03, 0.7) * mm});
            skLineSegment(sketch, "E813", {"start": v(0.03, 0.7) * mm, "end": v(0.07, 0.7) * mm});
            skLineSegment(sketch, "E814", {"start": v(0.07, 0.7) * mm, "end": v(0.08, 0.66) * mm});
            skLineSegment(sketch, "E815", {"start": v(0.08, 0.66) * mm, "end": v(0.06, 0.62) * mm});
            skLineSegment(sketch, "E816", {"start": v(0.06, 0.62) * mm, "end": v(0.03, 0.6) * mm});
            skLineSegment(sketch, "E817", {"start": v(0.03, 0.6) * mm, "end": v(0.01, 0.57) * mm});
            skLineSegment(sketch, "E818", {"start": v(0.01, 0.57) * mm, "end": v(-0.01, 0.54) * mm});
            skLineSegment(sketch, "E819", {"start": v(-0.01, 0.54) * mm, "end": v(-0.04, 0.51) * mm});
            skLineSegment(sketch, "E820", {"start": v(-0.04, 0.51) * mm, "end": v(-0.06, 0.49) * mm});
            skLineSegment(sketch, "E821", {"start": v(-0.06, 0.49) * mm, "end": v(-0.1, 0.46) * mm});
            skLineSegment(sketch, "E822", {"start": v(-0.1, 0.46) * mm, "end": v(-0.12, 0.44) * mm});
            skLineSegment(sketch, "E823", {"start": v(-0.12, 0.44) * mm, "end": v(-0.14, 0.42) * mm});
            skLineSegment(sketch, "E824", {"start": v(-0.14, 0.42) * mm, "end": v(-0.17, 0.4) * mm});
            skLineSegment(sketch, "E825", {"start": v(-0.17, 0.4) * mm, "end": v(-0.2, 0.38) * mm});
            skLineSegment(sketch, "E826", {"start": v(-0.2, 0.38) * mm, "end": v(-0.21, 0.38) * mm});
            skLineSegment(sketch, "E827", {"start": v(-0.21, 0.38) * mm, "end": v(-0.23, 0.37) * mm});
            skLineSegment(sketch, "E828", {"start": v(-0.23, 0.37) * mm, "end": v(-0.24, 0.36) * mm});
            skLineSegment(sketch, "E829", {"start": v(-0.24, 0.36) * mm, "end": v(-0.25, 0.35) * mm});
            skLineSegment(sketch, "E830", {"start": v(-0.25, 0.35) * mm, "end": v(-0.26, 0.35) * mm});
            skLineSegment(sketch, "E831", {"start": v(-0.26, 0.35) * mm, "end": v(-0.26, 0.35) * mm});
            skLineSegment(sketch, "E832", {"start": v(-0.26, 0.35) * mm, "end": v(-0.27, 0.34) * mm});
            skLineSegment(sketch, "E833", {"start": v(-0.27, 0.34) * mm, "end": v(-0.28, 0.34) * mm});
            skLineSegment(sketch, "E834", {"start": v(-0.28, 0.34) * mm, "end": v(-0.29, 0.34) * mm});
            skLineSegment(sketch, "E835", {"start": v(-0.29, 0.34) * mm, "end": v(-0.26, 0.2) * mm});
            skCircle(sketch, "E836", {"center": v(-2, 0) * mm, "radius": 0.3 * mm});
            skLineSegment(sketch, "E837", {"start": v(-2, 1.15) * mm, "end": v(-2, -1.14) * mm, "construction": true});
            skLineSegment(sketch, "E838", {"start": v(-3.01, 0) * mm, "end": v(-1.08, 0) * mm, "construction": true});
            skLineSegment(sketch, "E839", {"start": v(-2.51, 0.14) * mm, "end": v(-1.38, 0.14) * mm, "construction": true});
            skLineSegment(sketch, "E840", {"start": v(-2.27, 0.14) * mm, "end": v(-1.73, 0.14) * mm});
            skSolve(sketch);
        }
        {
            var Q0;
            Q0=makeQuery(id+"F16.imprint","IMPRINT",FACE,{"disambiguationData":[TD([[makeQuery(id+"F16.imprint","IMPRINT",EDGE,{"derivedFrom":sQuery(id+"F16.wireOp",EDGE,"E12")}),-1.0]])]});
            var Q1;
            {var subQ0=sQuery(id+"F16.wireOp",EDGE,"E840");Q1=makeQuery(id+"F16.imprint","IMPRINT",FACE,{"disambiguationData":[TD([[makeQuery(id+"F16.imprint","IMPRINT",EDGE,{"derivedFrom":subQ0}),1.0]])]});}
            extrude(context, id + "F17", {"entities" : qUnion([Q0, Q1]), "depth" : 1 * mm});
        }
        {
            var Q0;
            Q0=makeQuery(id+"F17.opExtrude","SWEPT_BODY",BODY,{"disambiguationData":[OSD([sQuery(id+"F16.wireOp",EDGE,"E12"),sQuery(id+"F16.wireOp",EDGE,"E13"),sQuery(id+"F16.wireOp",EDGE,"E14"),sQuery(id+"F16.wireOp",EDGE,"E15"),sQuery(id+"F16.wireOp",EDGE,"E16"),sQuery(id+"F16.wireOp",EDGE,"E17"),sQuery(id+"F16.wireOp",EDGE,"E18"),sQuery(id+"F16.wireOp",EDGE,"E19"),sQuery(id+"F16.wireOp",EDGE,"E20"),sQuery(id+"F16.wireOp",EDGE,"E21"),sQuery(id+"F16.wireOp",EDGE,"E22"),sQuery(id+"F16.wireOp",EDGE,"E23"),sQuery(id+"F16.wireOp",EDGE,"E24"),sQuery(id+"F16.wireOp",EDGE,"E25"),sQuery(id+"F16.wireOp",EDGE,"E26"),sQuery(id+"F16.wireOp",EDGE,"E27"),sQuery(id+"F16.wireOp",EDGE,"E28"),sQuery(id+"F16.wireOp",EDGE,"E29"),sQuery(id+"F16.wireOp",EDGE,"E30"),sQuery(id+"F16.wireOp",EDGE,"E31"),sQuery(id+"F16.wireOp",EDGE,"E32"),sQuery(id+"F16.wireOp",EDGE,"E33"),sQuery(id+"F16.wireOp",EDGE,"E34"),sQuery(id+"F16.wireOp",EDGE,"E35"),sQuery(id+"F16.wireOp",EDGE,"E36"),sQuery(id+"F16.wireOp",EDGE,"E37"),sQuery(id+"F16.wireOp",EDGE,"E38"),sQuery(id+"F16.wireOp",EDGE,"E39"),sQuery(id+"F16.wireOp",EDGE,"E40"),sQuery(id+"F16.wireOp",EDGE,"E41"),sQuery(id+"F16.wireOp",EDGE,"E42"),sQuery(id+"F16.wireOp",EDGE,"E43"),sQuery(id+"F16.wireOp",EDGE,"E44"),sQuery(id+"F16.wireOp",EDGE,"E45"),sQuery(id+"F16.wireOp",EDGE,"E46"),sQuery(id+"F16.wireOp",EDGE,"E47"),sQuery(id+"F16.wireOp",EDGE,"E48"),sQuery(id+"F16.wireOp",EDGE,"E49"),sQuery(id+"F16.wireOp",EDGE,"E50"),sQuery(id+"F16.wireOp",EDGE,"E51"),sQuery(id+"F16.wireOp",EDGE,"E52"),sQuery(id+"F16.wireOp",EDGE,"E53"),sQuery(id+"F16.wireOp",EDGE,"E54"),sQuery(id+"F16.wireOp",EDGE,"E55"),sQuery(id+"F16.wireOp",EDGE,"E56"),sQuery(id+"F16.wireOp",EDGE,"E57"),sQuery(id+"F16.wireOp",EDGE,"E58"),sQuery(id+"F16.wireOp",EDGE,"E59"),sQuery(id+"F16.wireOp",EDGE,"E60"),sQuery(id+"F16.wireOp",EDGE,"E61"),sQuery(id+"F16.wireOp",EDGE,"E62"),sQuery(id+"F16.wireOp",EDGE,"E63"),sQuery(id+"F16.wireOp",EDGE,"E64"),sQuery(id+"F16.wireOp",EDGE,"E65"),sQuery(id+"F16.wireOp",EDGE,"E66"),sQuery(id+"F16.wireOp",EDGE,"E67"),sQuery(id+"F16.wireOp",EDGE,"E68"),sQuery(id+"F16.wireOp",EDGE,"E69"),sQuery(id+"F16.wireOp",EDGE,"E70"),sQuery(id+"F16.wireOp",EDGE,"E71"),sQuery(id+"F16.wireOp",EDGE,"E72"),sQuery(id+"F16.wireOp",EDGE,"E73"),sQuery(id+"F16.wireOp",EDGE,"E74"),sQuery(id+"F16.wireOp",EDGE,"E75"),sQuery(id+"F16.wireOp",EDGE,"E76"),sQuery(id+"F16.wireOp",EDGE,"E77"),sQuery(id+"F16.wireOp",EDGE,"E78"),sQuery(id+"F16.wireOp",EDGE,"E79"),sQuery(id+"F16.wireOp",EDGE,"E80"),sQuery(id+"F16.wireOp",EDGE,"E81"),sQuery(id+"F16.wireOp",EDGE,"E82"),sQuery(id+"F16.wireOp",EDGE,"E83"),sQuery(id+"F16.wireOp",EDGE,"E84"),sQuery(id+"F16.wireOp",EDGE,"E85"),sQuery(id+"F16.wireOp",EDGE,"E86"),sQuery(id+"F16.wireOp",EDGE,"E87"),sQuery(id+"F16.wireOp",EDGE,"E88"),sQuery(id+"F16.wireOp",EDGE,"E89"),sQuery(id+"F16.wireOp",EDGE,"E90"),sQuery(id+"F16.wireOp",EDGE,"E91"),sQuery(id+"F16.wireOp",EDGE,"E92"),sQuery(id+"F16.wireOp",EDGE,"E92"),sQuery(id+"F16.wireOp",EDGE,"E93"),sQuery(id+"F16.wireOp",EDGE,"E94"),sQuery(id+"F16.wireOp",EDGE,"E95"),sQuery(id+"F16.wireOp",EDGE,"E96"),sQuery(id+"F16.wireOp",EDGE,"E97"),sQuery(id+"F16.wireOp",EDGE,"E98"),sQuery(id+"F16.wireOp",EDGE,"E99"),sQuery(id+"F16.wireOp",EDGE,"E100"),sQuery(id+"F16.wireOp",EDGE,"E101"),sQuery(id+"F16.wireOp",EDGE,"E102"),sQuery(id+"F16.wireOp",EDGE,"E103"),sQuery(id+"F16.wireOp",EDGE,"E104"),sQuery(id+"F16.wireOp",EDGE,"E105"),sQuery(id+"F16.wireOp",EDGE,"E106"),sQuery(id+"F16.wireOp",EDGE,"E107"),sQuery(id+"F16.wireOp",EDGE,"E108"),sQuery(id+"F16.wireOp",EDGE,"E109"),sQuery(id+"F16.wireOp",EDGE,"E110"),sQuery(id+"F16.wireOp",EDGE,"E111"),sQuery(id+"F16.wireOp",EDGE,"E112"),sQuery(id+"F16.wireOp",EDGE,"E113"),sQuery(id+"F16.wireOp",EDGE,"E114"),sQuery(id+"F16.wireOp",EDGE,"E115"),sQuery(id+"F16.wireOp",EDGE,"E116"),sQuery(id+"F16.wireOp",EDGE,"E117"),sQuery(id+"F16.wireOp",EDGE,"E118"),sQuery(id+"F16.wireOp",EDGE,"E119"),sQuery(id+"F16.wireOp",EDGE,"E120"),sQuery(id+"F16.wireOp",EDGE,"E121"),sQuery(id+"F16.wireOp",EDGE,"E122"),sQuery(id+"F16.wireOp",EDGE,"E123"),sQuery(id+"F16.wireOp",EDGE,"E124"),sQuery(id+"F16.wireOp",EDGE,"E125"),sQuery(id+"F16.wireOp",EDGE,"E126"),sQuery(id+"F16.wireOp",EDGE,"E127"),sQuery(id+"F16.wireOp",EDGE,"E128"),sQuery(id+"F16.wireOp",EDGE,"E129"),sQuery(id+"F16.wireOp",EDGE,"E130"),sQuery(id+"F16.wireOp",EDGE,"E131"),sQuery(id+"F16.wireOp",EDGE,"E132"),sQuery(id+"F16.wireOp",EDGE,"E132"),sQuery(id+"F16.wireOp",EDGE,"E133"),sQuery(id+"F16.wireOp",EDGE,"E134"),sQuery(id+"F16.wireOp",EDGE,"E135"),sQuery(id+"F16.wireOp",EDGE,"E136"),sQuery(id+"F16.wireOp",EDGE,"E137"),sQuery(id+"F16.wireOp",EDGE,"E138"),sQuery(id+"F16.wireOp",EDGE,"E138"),sQuery(id+"F16.wireOp",EDGE,"E139"),sQuery(id+"F16.wireOp",EDGE,"E140"),sQuery(id+"F16.wireOp",EDGE,"E141"),sQuery(id+"F16.wireOp",EDGE,"E142"),sQuery(id+"F16.wireOp",EDGE,"E143"),sQuery(id+"F16.wireOp",EDGE,"E144"),sQuery(id+"F16.wireOp",EDGE,"E145"),sQuery(id+"F16.wireOp",EDGE,"E146"),sQuery(id+"F16.wireOp",EDGE,"E147"),sQuery(id+"F16.wireOp",EDGE,"E148"),sQuery(id+"F16.wireOp",EDGE,"E149"),sQuery(id+"F16.wireOp",EDGE,"E150"),sQuery(id+"F16.wireOp",EDGE,"E151"),sQuery(id+"F16.wireOp",EDGE,"E152"),sQuery(id+"F16.wireOp",EDGE,"E153"),sQuery(id+"F16.wireOp",EDGE,"E154"),sQuery(id+"F16.wireOp",EDGE,"E155"),sQuery(id+"F16.wireOp",EDGE,"E156"),sQuery(id+"F16.wireOp",EDGE,"E157"),sQuery(id+"F16.wireOp",EDGE,"E158"),sQuery(id+"F16.wireOp",EDGE,"E159"),sQuery(id+"F16.wireOp",EDGE,"E160"),sQuery(id+"F16.wireOp",EDGE,"E161"),sQuery(id+"F16.wireOp",EDGE,"E162"),sQuery(id+"F16.wireOp",EDGE,"E163"),sQuery(id+"F16.wireOp",EDGE,"E164"),sQuery(id+"F16.wireOp",EDGE,"E165"),sQuery(id+"F16.wireOp",EDGE,"E166"),sQuery(id+"F16.wireOp",EDGE,"E167"),sQuery(id+"F16.wireOp",EDGE,"E168"),sQuery(id+"F16.wireOp",EDGE,"E169"),sQuery(id+"F16.wireOp",EDGE,"E170"),sQuery(id+"F16.wireOp",EDGE,"E171"),sQuery(id+"F16.wireOp",EDGE,"E172"),sQuery(id+"F16.wireOp",EDGE,"E173"),sQuery(id+"F16.wireOp",EDGE,"E174"),sQuery(id+"F16.wireOp",EDGE,"E175"),sQuery(id+"F16.wireOp",EDGE,"E176"),sQuery(id+"F16.wireOp",EDGE,"E177"),sQuery(id+"F16.wireOp",EDGE,"E178"),sQuery(id+"F16.wireOp",EDGE,"E178"),sQuery(id+"F16.wireOp",EDGE,"E179"),sQuery(id+"F16.wireOp",EDGE,"E180"),sQuery(id+"F16.wireOp",EDGE,"E181"),sQuery(id+"F16.wireOp",EDGE,"E182"),sQuery(id+"F16.wireOp",EDGE,"E183"),sQuery(id+"F16.wireOp",EDGE,"E184"),sQuery(id+"F16.wireOp",EDGE,"E185"),sQuery(id+"F16.wireOp",EDGE,"E186"),sQuery(id+"F16.wireOp",EDGE,"E187"),sQuery(id+"F16.wireOp",EDGE,"E188"),sQuery(id+"F16.wireOp",EDGE,"E189"),sQuery(id+"F16.wireOp",EDGE,"E190"),sQuery(id+"F16.wireOp",EDGE,"E191"),sQuery(id+"F16.wireOp",EDGE,"E192"),sQuery(id+"F16.wireOp",EDGE,"E193"),sQuery(id+"F16.wireOp",EDGE,"E194"),sQuery(id+"F16.wireOp",EDGE,"E195"),sQuery(id+"F16.wireOp",EDGE,"E196"),sQuery(id+"F16.wireOp",EDGE,"E197"),sQuery(id+"F16.wireOp",EDGE,"E198"),sQuery(id+"F16.wireOp",EDGE,"E199"),sQuery(id+"F16.wireOp",EDGE,"E200"),sQuery(id+"F16.wireOp",EDGE,"E201"),sQuery(id+"F16.wireOp",EDGE,"E202"),sQuery(id+"F16.wireOp",EDGE,"E203"),sQuery(id+"F16.wireOp",EDGE,"E204"),sQuery(id+"F16.wireOp",EDGE,"E205"),sQuery(id+"F16.wireOp",EDGE,"E206"),sQuery(id+"F16.wireOp",EDGE,"E207"),sQuery(id+"F16.wireOp",EDGE,"E208"),sQuery(id+"F16.wireOp",EDGE,"E209"),sQuery(id+"F16.wireOp",EDGE,"E210"),sQuery(id+"F16.wireOp",EDGE,"E211"),sQuery(id+"F16.wireOp",EDGE,"E212"),sQuery(id+"F16.wireOp",EDGE,"E213"),sQuery(id+"F16.wireOp",EDGE,"E214"),sQuery(id+"F16.wireOp",EDGE,"E215"),sQuery(id+"F16.wireOp",EDGE,"E216"),sQuery(id+"F16.wireOp",EDGE,"E217"),sQuery(id+"F16.wireOp",EDGE,"E218"),sQuery(id+"F16.wireOp",EDGE,"E219"),sQuery(id+"F16.wireOp",EDGE,"E220"),sQuery(id+"F16.wireOp",EDGE,"E221"),sQuery(id+"F16.wireOp",EDGE,"E222"),sQuery(id+"F16.wireOp",EDGE,"E223"),sQuery(id+"F16.wireOp",EDGE,"E224"),sQuery(id+"F16.wireOp",EDGE,"E225"),sQuery(id+"F16.wireOp",EDGE,"E226"),sQuery(id+"F16.wireOp",EDGE,"E227"),sQuery(id+"F16.wireOp",EDGE,"E228"),sQuery(id+"F16.wireOp",EDGE,"E229"),sQuery(id+"F16.wireOp",EDGE,"E230"),sQuery(id+"F16.wireOp",EDGE,"E231"),sQuery(id+"F16.wireOp",EDGE,"E232"),sQuery(id+"F16.wireOp",EDGE,"E233"),sQuery(id+"F16.wireOp",EDGE,"E234"),sQuery(id+"F16.wireOp",EDGE,"E235"),sQuery(id+"F16.wireOp",EDGE,"E236"),sQuery(id+"F16.wireOp",EDGE,"E237"),sQuery(id+"F16.wireOp",EDGE,"E238"),sQuery(id+"F16.wireOp",EDGE,"E239"),sQuery(id+"F16.wireOp",EDGE,"E240"),sQuery(id+"F16.wireOp",EDGE,"E241"),sQuery(id+"F16.wireOp",EDGE,"E242"),sQuery(id+"F16.wireOp",EDGE,"E243"),sQuery(id+"F16.wireOp",EDGE,"E244"),sQuery(id+"F16.wireOp",EDGE,"E245"),sQuery(id+"F16.wireOp",EDGE,"E246"),sQuery(id+"F16.wireOp",EDGE,"E247"),sQuery(id+"F16.wireOp",EDGE,"E248"),sQuery(id+"F16.wireOp",EDGE,"E249"),sQuery(id+"F16.wireOp",EDGE,"E250"),sQuery(id+"F16.wireOp",EDGE,"E251"),sQuery(id+"F16.wireOp",EDGE,"E252"),sQuery(id+"F16.wireOp",EDGE,"E253"),sQuery(id+"F16.wireOp",EDGE,"E254"),sQuery(id+"F16.wireOp",EDGE,"E255"),sQuery(id+"F16.wireOp",EDGE,"E256"),sQuery(id+"F16.wireOp",EDGE,"E257"),sQuery(id+"F16.wireOp",EDGE,"E258"),sQuery(id+"F16.wireOp",EDGE,"E259"),sQuery(id+"F16.wireOp",EDGE,"E260"),sQuery(id+"F16.wireOp",EDGE,"E261"),sQuery(id+"F16.wireOp",EDGE,"E262"),sQuery(id+"F16.wireOp",EDGE,"E263"),sQuery(id+"F16.wireOp",EDGE,"E264"),sQuery(id+"F16.wireOp",EDGE,"E265"),sQuery(id+"F16.wireOp",EDGE,"E266"),sQuery(id+"F16.wireOp",EDGE,"E267"),sQuery(id+"F16.wireOp",EDGE,"E268"),sQuery(id+"F16.wireOp",EDGE,"E269"),sQuery(id+"F16.wireOp",EDGE,"E270"),sQuery(id+"F16.wireOp",EDGE,"E271"),sQuery(id+"F16.wireOp",EDGE,"E272"),sQuery(id+"F16.wireOp",EDGE,"E273"),sQuery(id+"F16.wireOp",EDGE,"E274"),sQuery(id+"F16.wireOp",EDGE,"E275"),sQuery(id+"F16.wireOp",EDGE,"E276"),sQuery(id+"F16.wireOp",EDGE,"E277"),sQuery(id+"F16.wireOp",EDGE,"E278"),sQuery(id+"F16.wireOp",EDGE,"E279"),sQuery(id+"F16.wireOp",EDGE,"E280"),sQuery(id+"F16.wireOp",EDGE,"E281"),sQuery(id+"F16.wireOp",EDGE,"E282"),sQuery(id+"F16.wireOp",EDGE,"E283"),sQuery(id+"F16.wireOp",EDGE,"E284"),sQuery(id+"F16.wireOp",EDGE,"E285"),sQuery(id+"F16.wireOp",EDGE,"E286"),sQuery(id+"F16.wireOp",EDGE,"E287"),sQuery(id+"F16.wireOp",EDGE,"E288"),sQuery(id+"F16.wireOp",EDGE,"E289"),sQuery(id+"F16.wireOp",EDGE,"E290"),sQuery(id+"F16.wireOp",EDGE,"E291"),sQuery(id+"F16.wireOp",EDGE,"E292"),sQuery(id+"F16.wireOp",EDGE,"E293"),sQuery(id+"F16.wireOp",EDGE,"E294"),sQuery(id+"F16.wireOp",EDGE,"E295"),sQuery(id+"F16.wireOp",EDGE,"E296"),sQuery(id+"F16.wireOp",EDGE,"E297"),sQuery(id+"F16.wireOp",EDGE,"E298"),sQuery(id+"F16.wireOp",EDGE,"E298"),sQuery(id+"F16.wireOp",EDGE,"E299"),sQuery(id+"F16.wireOp",EDGE,"E300"),sQuery(id+"F16.wireOp",EDGE,"E301"),sQuery(id+"F16.wireOp",EDGE,"E302"),sQuery(id+"F16.wireOp",EDGE,"E303"),sQuery(id+"F16.wireOp",EDGE,"E304"),sQuery(id+"F16.wireOp",EDGE,"E305"),sQuery(id+"F16.wireOp",EDGE,"E306"),sQuery(id+"F16.wireOp",EDGE,"E307"),sQuery(id+"F16.wireOp",EDGE,"E308"),sQuery(id+"F16.wireOp",EDGE,"E309"),sQuery(id+"F16.wireOp",EDGE,"E310"),sQuery(id+"F16.wireOp",EDGE,"E311"),sQuery(id+"F16.wireOp",EDGE,"E312"),sQuery(id+"F16.wireOp",EDGE,"E313"),sQuery(id+"F16.wireOp",EDGE,"E314"),sQuery(id+"F16.wireOp",EDGE,"E315"),sQuery(id+"F16.wireOp",EDGE,"E316"),sQuery(id+"F16.wireOp",EDGE,"E317"),sQuery(id+"F16.wireOp",EDGE,"E318"),sQuery(id+"F16.wireOp",EDGE,"E319"),sQuery(id+"F16.wireOp",EDGE,"E320"),sQuery(id+"F16.wireOp",EDGE,"E321"),sQuery(id+"F16.wireOp",EDGE,"E322"),sQuery(id+"F16.wireOp",EDGE,"E323"),sQuery(id+"F16.wireOp",EDGE,"E324"),sQuery(id+"F16.wireOp",EDGE,"E325"),sQuery(id+"F16.wireOp",EDGE,"E326"),sQuery(id+"F16.wireOp",EDGE,"E327"),sQuery(id+"F16.wireOp",EDGE,"E328"),sQuery(id+"F16.wireOp",EDGE,"E329"),sQuery(id+"F16.wireOp",EDGE,"E330"),sQuery(id+"F16.wireOp",EDGE,"E331"),sQuery(id+"F16.wireOp",EDGE,"E332"),sQuery(id+"F16.wireOp",EDGE,"E333"),sQuery(id+"F16.wireOp",EDGE,"E334"),sQuery(id+"F16.wireOp",EDGE,"E335"),sQuery(id+"F16.wireOp",EDGE,"E336"),sQuery(id+"F16.wireOp",EDGE,"E337"),sQuery(id+"F16.wireOp",EDGE,"E338"),sQuery(id+"F16.wireOp",EDGE,"E338"),sQuery(id+"F16.wireOp",EDGE,"E339"),sQuery(id+"F16.wireOp",EDGE,"E340"),sQuery(id+"F16.wireOp",EDGE,"E341"),sQuery(id+"F16.wireOp",EDGE,"E342"),sQuery(id+"F16.wireOp",EDGE,"E343"),sQuery(id+"F16.wireOp",EDGE,"E344"),sQuery(id+"F16.wireOp",EDGE,"E344"),sQuery(id+"F16.wireOp",EDGE,"E345"),sQuery(id+"F16.wireOp",EDGE,"E346"),sQuery(id+"F16.wireOp",EDGE,"E347"),sQuery(id+"F16.wireOp",EDGE,"E348"),sQuery(id+"F16.wireOp",EDGE,"E349"),sQuery(id+"F16.wireOp",EDGE,"E350"),sQuery(id+"F16.wireOp",EDGE,"E351"),sQuery(id+"F16.wireOp",EDGE,"E352"),sQuery(id+"F16.wireOp",EDGE,"E353"),sQuery(id+"F16.wireOp",EDGE,"E354"),sQuery(id+"F16.wireOp",EDGE,"E355"),sQuery(id+"F16.wireOp",EDGE,"E356"),sQuery(id+"F16.wireOp",EDGE,"E357"),sQuery(id+"F16.wireOp",EDGE,"E358"),sQuery(id+"F16.wireOp",EDGE,"E359"),sQuery(id+"F16.wireOp",EDGE,"E360"),sQuery(id+"F16.wireOp",EDGE,"E361"),sQuery(id+"F16.wireOp",EDGE,"E362"),sQuery(id+"F16.wireOp",EDGE,"E363"),sQuery(id+"F16.wireOp",EDGE,"E364"),sQuery(id+"F16.wireOp",EDGE,"E365"),sQuery(id+"F16.wireOp",EDGE,"E366"),sQuery(id+"F16.wireOp",EDGE,"E367"),sQuery(id+"F16.wireOp",EDGE,"E368"),sQuery(id+"F16.wireOp",EDGE,"E369"),sQuery(id+"F16.wireOp",EDGE,"E370"),sQuery(id+"F16.wireOp",EDGE,"E371"),sQuery(id+"F16.wireOp",EDGE,"E372"),sQuery(id+"F16.wireOp",EDGE,"E373"),sQuery(id+"F16.wireOp",EDGE,"E374"),sQuery(id+"F16.wireOp",EDGE,"E375"),sQuery(id+"F16.wireOp",EDGE,"E376"),sQuery(id+"F16.wireOp",EDGE,"E377"),sQuery(id+"F16.wireOp",EDGE,"E378"),sQuery(id+"F16.wireOp",EDGE,"E379"),sQuery(id+"F16.wireOp",EDGE,"E380"),sQuery(id+"F16.wireOp",EDGE,"E381"),sQuery(id+"F16.wireOp",EDGE,"E382"),sQuery(id+"F16.wireOp",EDGE,"E383"),sQuery(id+"F16.wireOp",EDGE,"E384"),sQuery(id+"F16.wireOp",EDGE,"E384"),sQuery(id+"F16.wireOp",EDGE,"E385"),sQuery(id+"F16.wireOp",EDGE,"E386"),sQuery(id+"F16.wireOp",EDGE,"E387"),sQuery(id+"F16.wireOp",EDGE,"E388"),sQuery(id+"F16.wireOp",EDGE,"E389"),sQuery(id+"F16.wireOp",EDGE,"E390"),sQuery(id+"F16.wireOp",EDGE,"E391"),sQuery(id+"F16.wireOp",EDGE,"E392"),sQuery(id+"F16.wireOp",EDGE,"E393"),sQuery(id+"F16.wireOp",EDGE,"E394"),sQuery(id+"F16.wireOp",EDGE,"E395"),sQuery(id+"F16.wireOp",EDGE,"E396"),sQuery(id+"F16.wireOp",EDGE,"E397"),sQuery(id+"F16.wireOp",EDGE,"E398"),sQuery(id+"F16.wireOp",EDGE,"E399"),sQuery(id+"F16.wireOp",EDGE,"E400"),sQuery(id+"F16.wireOp",EDGE,"E401"),sQuery(id+"F16.wireOp",EDGE,"E402"),sQuery(id+"F16.wireOp",EDGE,"E403"),sQuery(id+"F16.wireOp",EDGE,"E404"),sQuery(id+"F16.wireOp",EDGE,"E405"),sQuery(id+"F16.wireOp",EDGE,"E406"),sQuery(id+"F16.wireOp",EDGE,"E407"),sQuery(id+"F16.wireOp",EDGE,"E408"),sQuery(id+"F16.wireOp",EDGE,"E409"),sQuery(id+"F16.wireOp",EDGE,"E410"),sQuery(id+"F16.wireOp",EDGE,"E411"),sQuery(id+"F16.wireOp",EDGE,"E412"),sQuery(id+"F16.wireOp",EDGE,"E413"),sQuery(id+"F16.wireOp",EDGE,"E414"),sQuery(id+"F16.wireOp",EDGE,"E415"),sQuery(id+"F16.wireOp",EDGE,"E416"),sQuery(id+"F16.wireOp",EDGE,"E417"),sQuery(id+"F16.wireOp",EDGE,"E418"),sQuery(id+"F16.wireOp",EDGE,"E419"),sQuery(id+"F16.wireOp",EDGE,"E420"),sQuery(id+"F16.wireOp",EDGE,"E421"),sQuery(id+"F16.wireOp",EDGE,"E422"),sQuery(id+"F16.wireOp",EDGE,"E423"),sQuery(id+"F16.wireOp",EDGE,"E424"),sQuery(id+"F16.wireOp",EDGE,"E425"),sQuery(id+"F16.wireOp",EDGE,"E426"),sQuery(id+"F16.wireOp",EDGE,"E427"),sQuery(id+"F16.wireOp",EDGE,"E428"),sQuery(id+"F16.wireOp",EDGE,"E429"),sQuery(id+"F16.wireOp",EDGE,"E430"),sQuery(id+"F16.wireOp",EDGE,"E431"),sQuery(id+"F16.wireOp",EDGE,"E432"),sQuery(id+"F16.wireOp",EDGE,"E433"),sQuery(id+"F16.wireOp",EDGE,"E434"),sQuery(id+"F16.wireOp",EDGE,"E435"),sQuery(id+"F16.wireOp",EDGE,"E436"),sQuery(id+"F16.wireOp",EDGE,"E437"),sQuery(id+"F16.wireOp",EDGE,"E438"),sQuery(id+"F16.wireOp",EDGE,"E439"),sQuery(id+"F16.wireOp",EDGE,"E440"),sQuery(id+"F16.wireOp",EDGE,"E441"),sQuery(id+"F16.wireOp",EDGE,"E442"),sQuery(id+"F16.wireOp",EDGE,"E443"),sQuery(id+"F16.wireOp",EDGE,"E444"),sQuery(id+"F16.wireOp",EDGE,"E445"),sQuery(id+"F16.wireOp",EDGE,"E446"),sQuery(id+"F16.wireOp",EDGE,"E447"),sQuery(id+"F16.wireOp",EDGE,"E448"),sQuery(id+"F16.wireOp",EDGE,"E449"),sQuery(id+"F16.wireOp",EDGE,"E450"),sQuery(id+"F16.wireOp",EDGE,"E451"),sQuery(id+"F16.wireOp",EDGE,"E452"),sQuery(id+"F16.wireOp",EDGE,"E453"),sQuery(id+"F16.wireOp",EDGE,"E454"),sQuery(id+"F16.wireOp",EDGE,"E455"),sQuery(id+"F16.wireOp",EDGE,"E456"),sQuery(id+"F16.wireOp",EDGE,"E457"),sQuery(id+"F16.wireOp",EDGE,"E458"),sQuery(id+"F16.wireOp",EDGE,"E459"),sQuery(id+"F16.wireOp",EDGE,"E460"),sQuery(id+"F16.wireOp",EDGE,"E461"),sQuery(id+"F16.wireOp",EDGE,"E462"),sQuery(id+"F16.wireOp",EDGE,"E463"),sQuery(id+"F16.wireOp",EDGE,"E464"),sQuery(id+"F16.wireOp",EDGE,"E465"),sQuery(id+"F16.wireOp",EDGE,"E466"),sQuery(id+"F16.wireOp",EDGE,"E467"),sQuery(id+"F16.wireOp",EDGE,"E468"),sQuery(id+"F16.wireOp",EDGE,"E469"),sQuery(id+"F16.wireOp",EDGE,"E470"),sQuery(id+"F16.wireOp",EDGE,"E471"),sQuery(id+"F16.wireOp",EDGE,"E472"),sQuery(id+"F16.wireOp",EDGE,"E473"),sQuery(id+"F16.wireOp",EDGE,"E474"),sQuery(id+"F16.wireOp",EDGE,"E475"),sQuery(id+"F16.wireOp",EDGE,"E476"),sQuery(id+"F16.wireOp",EDGE,"E477"),sQuery(id+"F16.wireOp",EDGE,"E478"),sQuery(id+"F16.wireOp",EDGE,"E479"),sQuery(id+"F16.wireOp",EDGE,"E480"),sQuery(id+"F16.wireOp",EDGE,"E481"),sQuery(id+"F16.wireOp",EDGE,"E482"),sQuery(id+"F16.wireOp",EDGE,"E483"),sQuery(id+"F16.wireOp",EDGE,"E484"),sQuery(id+"F16.wireOp",EDGE,"E485"),sQuery(id+"F16.wireOp",EDGE,"E486"),sQuery(id+"F16.wireOp",EDGE,"E487"),sQuery(id+"F16.wireOp",EDGE,"E488"),sQuery(id+"F16.wireOp",EDGE,"E489"),sQuery(id+"F16.wireOp",EDGE,"E490"),sQuery(id+"F16.wireOp",EDGE,"E491"),sQuery(id+"F16.wireOp",EDGE,"E492"),sQuery(id+"F16.wireOp",EDGE,"E493"),sQuery(id+"F16.wireOp",EDGE,"E494"),sQuery(id+"F16.wireOp",EDGE,"E495"),sQuery(id+"F16.wireOp",EDGE,"E496"),sQuery(id+"F16.wireOp",EDGE,"E497"),sQuery(id+"F16.wireOp",EDGE,"E498"),sQuery(id+"F16.wireOp",EDGE,"E499"),sQuery(id+"F16.wireOp",EDGE,"E500"),sQuery(id+"F16.wireOp",EDGE,"E501"),sQuery(id+"F16.wireOp",EDGE,"E502"),sQuery(id+"F16.wireOp",EDGE,"E503"),sQuery(id+"F16.wireOp",EDGE,"E504"),sQuery(id+"F16.wireOp",EDGE,"E504"),sQuery(id+"F16.wireOp",EDGE,"E505"),sQuery(id+"F16.wireOp",EDGE,"E506"),sQuery(id+"F16.wireOp",EDGE,"E507"),sQuery(id+"F16.wireOp",EDGE,"E508"),sQuery(id+"F16.wireOp",EDGE,"E509"),sQuery(id+"F16.wireOp",EDGE,"E510"),sQuery(id+"F16.wireOp",EDGE,"E511"),sQuery(id+"F16.wireOp",EDGE,"E512"),sQuery(id+"F16.wireOp",EDGE,"E513"),sQuery(id+"F16.wireOp",EDGE,"E514"),sQuery(id+"F16.wireOp",EDGE,"E515"),sQuery(id+"F16.wireOp",EDGE,"E516"),sQuery(id+"F16.wireOp",EDGE,"E517"),sQuery(id+"F16.wireOp",EDGE,"E518"),sQuery(id+"F16.wireOp",EDGE,"E519"),sQuery(id+"F16.wireOp",EDGE,"E520"),sQuery(id+"F16.wireOp",EDGE,"E521"),sQuery(id+"F16.wireOp",EDGE,"E522"),sQuery(id+"F16.wireOp",EDGE,"E523"),sQuery(id+"F16.wireOp",EDGE,"E524"),sQuery(id+"F16.wireOp",EDGE,"E525"),sQuery(id+"F16.wireOp",EDGE,"E526"),sQuery(id+"F16.wireOp",EDGE,"E527"),sQuery(id+"F16.wireOp",EDGE,"E528"),sQuery(id+"F16.wireOp",EDGE,"E529"),sQuery(id+"F16.wireOp",EDGE,"E530"),sQuery(id+"F16.wireOp",EDGE,"E531"),sQuery(id+"F16.wireOp",EDGE,"E532"),sQuery(id+"F16.wireOp",EDGE,"E533"),sQuery(id+"F16.wireOp",EDGE,"E534"),sQuery(id+"F16.wireOp",EDGE,"E535"),sQuery(id+"F16.wireOp",EDGE,"E536"),sQuery(id+"F16.wireOp",EDGE,"E537"),sQuery(id+"F16.wireOp",EDGE,"E538"),sQuery(id+"F16.wireOp",EDGE,"E539"),sQuery(id+"F16.wireOp",EDGE,"E540"),sQuery(id+"F16.wireOp",EDGE,"E541"),sQuery(id+"F16.wireOp",EDGE,"E542"),sQuery(id+"F16.wireOp",EDGE,"E543"),sQuery(id+"F16.wireOp",EDGE,"E544"),sQuery(id+"F16.wireOp",EDGE,"E544"),sQuery(id+"F16.wireOp",EDGE,"E545"),sQuery(id+"F16.wireOp",EDGE,"E546"),sQuery(id+"F16.wireOp",EDGE,"E547"),sQuery(id+"F16.wireOp",EDGE,"E548"),sQuery(id+"F16.wireOp",EDGE,"E549"),sQuery(id+"F16.wireOp",EDGE,"E550"),sQuery(id+"F16.wireOp",EDGE,"E550"),sQuery(id+"F16.wireOp",EDGE,"E551"),sQuery(id+"F16.wireOp",EDGE,"E552"),sQuery(id+"F16.wireOp",EDGE,"E553"),sQuery(id+"F16.wireOp",EDGE,"E554"),sQuery(id+"F16.wireOp",EDGE,"E555"),sQuery(id+"F16.wireOp",EDGE,"E556"),sQuery(id+"F16.wireOp",EDGE,"E557"),sQuery(id+"F16.wireOp",EDGE,"E558"),sQuery(id+"F16.wireOp",EDGE,"E559"),sQuery(id+"F16.wireOp",EDGE,"E560"),sQuery(id+"F16.wireOp",EDGE,"E561"),sQuery(id+"F16.wireOp",EDGE,"E562"),sQuery(id+"F16.wireOp",EDGE,"E563"),sQuery(id+"F16.wireOp",EDGE,"E564"),sQuery(id+"F16.wireOp",EDGE,"E565"),sQuery(id+"F16.wireOp",EDGE,"E566"),sQuery(id+"F16.wireOp",EDGE,"E567"),sQuery(id+"F16.wireOp",EDGE,"E568"),sQuery(id+"F16.wireOp",EDGE,"E569"),sQuery(id+"F16.wireOp",EDGE,"E570"),sQuery(id+"F16.wireOp",EDGE,"E571"),sQuery(id+"F16.wireOp",EDGE,"E572"),sQuery(id+"F16.wireOp",EDGE,"E573"),sQuery(id+"F16.wireOp",EDGE,"E574"),sQuery(id+"F16.wireOp",EDGE,"E575"),sQuery(id+"F16.wireOp",EDGE,"E576"),sQuery(id+"F16.wireOp",EDGE,"E577"),sQuery(id+"F16.wireOp",EDGE,"E578"),sQuery(id+"F16.wireOp",EDGE,"E579"),sQuery(id+"F16.wireOp",EDGE,"E580"),sQuery(id+"F16.wireOp",EDGE,"E581"),sQuery(id+"F16.wireOp",EDGE,"E582"),sQuery(id+"F16.wireOp",EDGE,"E583"),sQuery(id+"F16.wireOp",EDGE,"E584"),sQuery(id+"F16.wireOp",EDGE,"E585"),sQuery(id+"F16.wireOp",EDGE,"E586"),sQuery(id+"F16.wireOp",EDGE,"E587"),sQuery(id+"F16.wireOp",EDGE,"E588"),sQuery(id+"F16.wireOp",EDGE,"E589"),sQuery(id+"F16.wireOp",EDGE,"E590"),sQuery(id+"F16.wireOp",EDGE,"E590"),sQuery(id+"F16.wireOp",EDGE,"E591"),sQuery(id+"F16.wireOp",EDGE,"E592"),sQuery(id+"F16.wireOp",EDGE,"E593"),sQuery(id+"F16.wireOp",EDGE,"E594"),sQuery(id+"F16.wireOp",EDGE,"E595"),sQuery(id+"F16.wireOp",EDGE,"E596"),sQuery(id+"F16.wireOp",EDGE,"E597"),sQuery(id+"F16.wireOp",EDGE,"E598"),sQuery(id+"F16.wireOp",EDGE,"E599"),sQuery(id+"F16.wireOp",EDGE,"E600"),sQuery(id+"F16.wireOp",EDGE,"E601"),sQuery(id+"F16.wireOp",EDGE,"E602"),sQuery(id+"F16.wireOp",EDGE,"E603"),sQuery(id+"F16.wireOp",EDGE,"E604"),sQuery(id+"F16.wireOp",EDGE,"E605"),sQuery(id+"F16.wireOp",EDGE,"E606"),sQuery(id+"F16.wireOp",EDGE,"E607"),sQuery(id+"F16.wireOp",EDGE,"E608"),sQuery(id+"F16.wireOp",EDGE,"E609"),sQuery(id+"F16.wireOp",EDGE,"E610"),sQuery(id+"F16.wireOp",EDGE,"E611"),sQuery(id+"F16.wireOp",EDGE,"E612"),sQuery(id+"F16.wireOp",EDGE,"E613"),sQuery(id+"F16.wireOp",EDGE,"E614"),sQuery(id+"F16.wireOp",EDGE,"E615"),sQuery(id+"F16.wireOp",EDGE,"E616"),sQuery(id+"F16.wireOp",EDGE,"E617"),sQuery(id+"F16.wireOp",EDGE,"E618"),sQuery(id+"F16.wireOp",EDGE,"E619"),sQuery(id+"F16.wireOp",EDGE,"E620"),sQuery(id+"F16.wireOp",EDGE,"E621"),sQuery(id+"F16.wireOp",EDGE,"E622"),sQuery(id+"F16.wireOp",EDGE,"E623"),sQuery(id+"F16.wireOp",EDGE,"E624"),sQuery(id+"F16.wireOp",EDGE,"E625"),sQuery(id+"F16.wireOp",EDGE,"E626"),sQuery(id+"F16.wireOp",EDGE,"E627"),sQuery(id+"F16.wireOp",EDGE,"E628"),sQuery(id+"F16.wireOp",EDGE,"E629"),sQuery(id+"F16.wireOp",EDGE,"E630"),sQuery(id+"F16.wireOp",EDGE,"E631"),sQuery(id+"F16.wireOp",EDGE,"E632"),sQuery(id+"F16.wireOp",EDGE,"E633"),sQuery(id+"F16.wireOp",EDGE,"E634"),sQuery(id+"F16.wireOp",EDGE,"E635"),sQuery(id+"F16.wireOp",EDGE,"E636"),sQuery(id+"F16.wireOp",EDGE,"E637"),sQuery(id+"F16.wireOp",EDGE,"E638"),sQuery(id+"F16.wireOp",EDGE,"E639"),sQuery(id+"F16.wireOp",EDGE,"E640"),sQuery(id+"F16.wireOp",EDGE,"E641"),sQuery(id+"F16.wireOp",EDGE,"E642"),sQuery(id+"F16.wireOp",EDGE,"E643"),sQuery(id+"F16.wireOp",EDGE,"E644"),sQuery(id+"F16.wireOp",EDGE,"E645"),sQuery(id+"F16.wireOp",EDGE,"E646"),sQuery(id+"F16.wireOp",EDGE,"E647"),sQuery(id+"F16.wireOp",EDGE,"E648"),sQuery(id+"F16.wireOp",EDGE,"E649"),sQuery(id+"F16.wireOp",EDGE,"E650"),sQuery(id+"F16.wireOp",EDGE,"E651"),sQuery(id+"F16.wireOp",EDGE,"E652"),sQuery(id+"F16.wireOp",EDGE,"E653"),sQuery(id+"F16.wireOp",EDGE,"E654"),sQuery(id+"F16.wireOp",EDGE,"E655"),sQuery(id+"F16.wireOp",EDGE,"E656"),sQuery(id+"F16.wireOp",EDGE,"E657"),sQuery(id+"F16.wireOp",EDGE,"E658"),sQuery(id+"F16.wireOp",EDGE,"E659"),sQuery(id+"F16.wireOp",EDGE,"E660"),sQuery(id+"F16.wireOp",EDGE,"E661"),sQuery(id+"F16.wireOp",EDGE,"E662"),sQuery(id+"F16.wireOp",EDGE,"E663"),sQuery(id+"F16.wireOp",EDGE,"E664"),sQuery(id+"F16.wireOp",EDGE,"E665"),sQuery(id+"F16.wireOp",EDGE,"E666"),sQuery(id+"F16.wireOp",EDGE,"E667"),sQuery(id+"F16.wireOp",EDGE,"E668"),sQuery(id+"F16.wireOp",EDGE,"E669"),sQuery(id+"F16.wireOp",EDGE,"E670"),sQuery(id+"F16.wireOp",EDGE,"E671"),sQuery(id+"F16.wireOp",EDGE,"E672"),sQuery(id+"F16.wireOp",EDGE,"E673"),sQuery(id+"F16.wireOp",EDGE,"E674"),sQuery(id+"F16.wireOp",EDGE,"E675"),sQuery(id+"F16.wireOp",EDGE,"E676"),sQuery(id+"F16.wireOp",EDGE,"E677"),sQuery(id+"F16.wireOp",EDGE,"E678"),sQuery(id+"F16.wireOp",EDGE,"E679"),sQuery(id+"F16.wireOp",EDGE,"E680"),sQuery(id+"F16.wireOp",EDGE,"E681"),sQuery(id+"F16.wireOp",EDGE,"E682"),sQuery(id+"F16.wireOp",EDGE,"E683"),sQuery(id+"F16.wireOp",EDGE,"E684"),sQuery(id+"F16.wireOp",EDGE,"E685"),sQuery(id+"F16.wireOp",EDGE,"E686"),sQuery(id+"F16.wireOp",EDGE,"E687"),sQuery(id+"F16.wireOp",EDGE,"E688"),sQuery(id+"F16.wireOp",EDGE,"E689"),sQuery(id+"F16.wireOp",EDGE,"E690"),sQuery(id+"F16.wireOp",EDGE,"E691"),sQuery(id+"F16.wireOp",EDGE,"E692"),sQuery(id+"F16.wireOp",EDGE,"E693"),sQuery(id+"F16.wireOp",EDGE,"E694"),sQuery(id+"F16.wireOp",EDGE,"E695"),sQuery(id+"F16.wireOp",EDGE,"E696"),sQuery(id+"F16.wireOp",EDGE,"E697"),sQuery(id+"F16.wireOp",EDGE,"E698"),sQuery(id+"F16.wireOp",EDGE,"E699"),sQuery(id+"F16.wireOp",EDGE,"E700"),sQuery(id+"F16.wireOp",EDGE,"E701"),sQuery(id+"F16.wireOp",EDGE,"E702"),sQuery(id+"F16.wireOp",EDGE,"E703"),sQuery(id+"F16.wireOp",EDGE,"E704"),sQuery(id+"F16.wireOp",EDGE,"E705"),sQuery(id+"F16.wireOp",EDGE,"E706"),sQuery(id+"F16.wireOp",EDGE,"E707"),sQuery(id+"F16.wireOp",EDGE,"E708"),sQuery(id+"F16.wireOp",EDGE,"E709"),sQuery(id+"F16.wireOp",EDGE,"E710"),sQuery(id+"F16.wireOp",EDGE,"E710"),sQuery(id+"F16.wireOp",EDGE,"E711"),sQuery(id+"F16.wireOp",EDGE,"E712"),sQuery(id+"F16.wireOp",EDGE,"E713"),sQuery(id+"F16.wireOp",EDGE,"E714"),sQuery(id+"F16.wireOp",EDGE,"E715"),sQuery(id+"F16.wireOp",EDGE,"E716"),sQuery(id+"F16.wireOp",EDGE,"E717"),sQuery(id+"F16.wireOp",EDGE,"E718"),sQuery(id+"F16.wireOp",EDGE,"E719"),sQuery(id+"F16.wireOp",EDGE,"E720"),sQuery(id+"F16.wireOp",EDGE,"E721"),sQuery(id+"F16.wireOp",EDGE,"E722"),sQuery(id+"F16.wireOp",EDGE,"E723"),sQuery(id+"F16.wireOp",EDGE,"E724"),sQuery(id+"F16.wireOp",EDGE,"E725"),sQuery(id+"F16.wireOp",EDGE,"E726"),sQuery(id+"F16.wireOp",EDGE,"E727"),sQuery(id+"F16.wireOp",EDGE,"E728"),sQuery(id+"F16.wireOp",EDGE,"E729"),sQuery(id+"F16.wireOp",EDGE,"E730"),sQuery(id+"F16.wireOp",EDGE,"E731"),sQuery(id+"F16.wireOp",EDGE,"E732"),sQuery(id+"F16.wireOp",EDGE,"E733"),sQuery(id+"F16.wireOp",EDGE,"E734"),sQuery(id+"F16.wireOp",EDGE,"E735"),sQuery(id+"F16.wireOp",EDGE,"E736"),sQuery(id+"F16.wireOp",EDGE,"E737"),sQuery(id+"F16.wireOp",EDGE,"E738"),sQuery(id+"F16.wireOp",EDGE,"E739"),sQuery(id+"F16.wireOp",EDGE,"E740"),sQuery(id+"F16.wireOp",EDGE,"E741"),sQuery(id+"F16.wireOp",EDGE,"E742"),sQuery(id+"F16.wireOp",EDGE,"E743"),sQuery(id+"F16.wireOp",EDGE,"E744"),sQuery(id+"F16.wireOp",EDGE,"E745"),sQuery(id+"F16.wireOp",EDGE,"E746"),sQuery(id+"F16.wireOp",EDGE,"E747"),sQuery(id+"F16.wireOp",EDGE,"E748"),sQuery(id+"F16.wireOp",EDGE,"E749"),sQuery(id+"F16.wireOp",EDGE,"E750"),sQuery(id+"F16.wireOp",EDGE,"E750"),sQuery(id+"F16.wireOp",EDGE,"E751"),sQuery(id+"F16.wireOp",EDGE,"E752"),sQuery(id+"F16.wireOp",EDGE,"E753"),sQuery(id+"F16.wireOp",EDGE,"E754"),sQuery(id+"F16.wireOp",EDGE,"E755"),sQuery(id+"F16.wireOp",EDGE,"E756"),sQuery(id+"F16.wireOp",EDGE,"E756"),sQuery(id+"F16.wireOp",EDGE,"E757"),sQuery(id+"F16.wireOp",EDGE,"E758"),sQuery(id+"F16.wireOp",EDGE,"E759"),sQuery(id+"F16.wireOp",EDGE,"E760"),sQuery(id+"F16.wireOp",EDGE,"E761"),sQuery(id+"F16.wireOp",EDGE,"E762"),sQuery(id+"F16.wireOp",EDGE,"E763"),sQuery(id+"F16.wireOp",EDGE,"E764"),sQuery(id+"F16.wireOp",EDGE,"E765"),sQuery(id+"F16.wireOp",EDGE,"E766"),sQuery(id+"F16.wireOp",EDGE,"E767"),sQuery(id+"F16.wireOp",EDGE,"E768"),sQuery(id+"F16.wireOp",EDGE,"E769"),sQuery(id+"F16.wireOp",EDGE,"E770"),sQuery(id+"F16.wireOp",EDGE,"E771"),sQuery(id+"F16.wireOp",EDGE,"E772"),sQuery(id+"F16.wireOp",EDGE,"E773"),sQuery(id+"F16.wireOp",EDGE,"E774"),sQuery(id+"F16.wireOp",EDGE,"E775"),sQuery(id+"F16.wireOp",EDGE,"E776"),sQuery(id+"F16.wireOp",EDGE,"E777"),sQuery(id+"F16.wireOp",EDGE,"E778"),sQuery(id+"F16.wireOp",EDGE,"E779"),sQuery(id+"F16.wireOp",EDGE,"E780"),sQuery(id+"F16.wireOp",EDGE,"E781"),sQuery(id+"F16.wireOp",EDGE,"E782"),sQuery(id+"F16.wireOp",EDGE,"E783"),sQuery(id+"F16.wireOp",EDGE,"E784"),sQuery(id+"F16.wireOp",EDGE,"E785"),sQuery(id+"F16.wireOp",EDGE,"E786"),sQuery(id+"F16.wireOp",EDGE,"E787"),sQuery(id+"F16.wireOp",EDGE,"E788"),sQuery(id+"F16.wireOp",EDGE,"E789"),sQuery(id+"F16.wireOp",EDGE,"E790"),sQuery(id+"F16.wireOp",EDGE,"E791"),sQuery(id+"F16.wireOp",EDGE,"E792"),sQuery(id+"F16.wireOp",EDGE,"E793"),sQuery(id+"F16.wireOp",EDGE,"E794"),sQuery(id+"F16.wireOp",EDGE,"E795"),sQuery(id+"F16.wireOp",EDGE,"E796"),sQuery(id+"F16.wireOp",EDGE,"E796"),sQuery(id+"F16.wireOp",EDGE,"E797"),sQuery(id+"F16.wireOp",EDGE,"E798"),sQuery(id+"F16.wireOp",EDGE,"E799"),sQuery(id+"F16.wireOp",EDGE,"E800"),sQuery(id+"F16.wireOp",EDGE,"E801"),sQuery(id+"F16.wireOp",EDGE,"E802"),sQuery(id+"F16.wireOp",EDGE,"E803"),sQuery(id+"F16.wireOp",EDGE,"E804"),sQuery(id+"F16.wireOp",EDGE,"E805"),sQuery(id+"F16.wireOp",EDGE,"E806"),sQuery(id+"F16.wireOp",EDGE,"E807"),sQuery(id+"F16.wireOp",EDGE,"E808"),sQuery(id+"F16.wireOp",EDGE,"E809"),sQuery(id+"F16.wireOp",EDGE,"E810"),sQuery(id+"F16.wireOp",EDGE,"E811"),sQuery(id+"F16.wireOp",EDGE,"E812"),sQuery(id+"F16.wireOp",EDGE,"E813"),sQuery(id+"F16.wireOp",EDGE,"E814"),sQuery(id+"F16.wireOp",EDGE,"E815"),sQuery(id+"F16.wireOp",EDGE,"E816"),sQuery(id+"F16.wireOp",EDGE,"E817"),sQuery(id+"F16.wireOp",EDGE,"E818"),sQuery(id+"F16.wireOp",EDGE,"E819"),sQuery(id+"F16.wireOp",EDGE,"E820"),sQuery(id+"F16.wireOp",EDGE,"E821"),sQuery(id+"F16.wireOp",EDGE,"E822"),sQuery(id+"F16.wireOp",EDGE,"E823"),sQuery(id+"F16.wireOp",EDGE,"E824"),sQuery(id+"F16.wireOp",EDGE,"E825"),sQuery(id+"F16.wireOp",EDGE,"E826"),sQuery(id+"F16.wireOp",EDGE,"E827"),sQuery(id+"F16.wireOp",EDGE,"E828"),sQuery(id+"F16.wireOp",EDGE,"E829"),sQuery(id+"F16.wireOp",EDGE,"E830"),sQuery(id+"F16.wireOp",EDGE,"E831"),sQuery(id+"F16.wireOp",EDGE,"E832"),sQuery(id+"F16.wireOp",EDGE,"E833"),sQuery(id+"F16.wireOp",EDGE,"E834"),sQuery(id+"F16.wireOp",EDGE,"E835"),sQuery(id+"F16.wireOp",EDGE,"E836")])]});
            var Q1;
            Q1=qCreatedBy(makeId("Origin.pointOp"),VERTEX);
            transform(context, id + "F18", {"entities" : qUnion([Q0]), "transformType" : TransformType.SCALE_UNIFORMLY, "scale" : 10, "scalePoint" : qUnion([Q1]), "makeCopy" : false});
        }
    });
